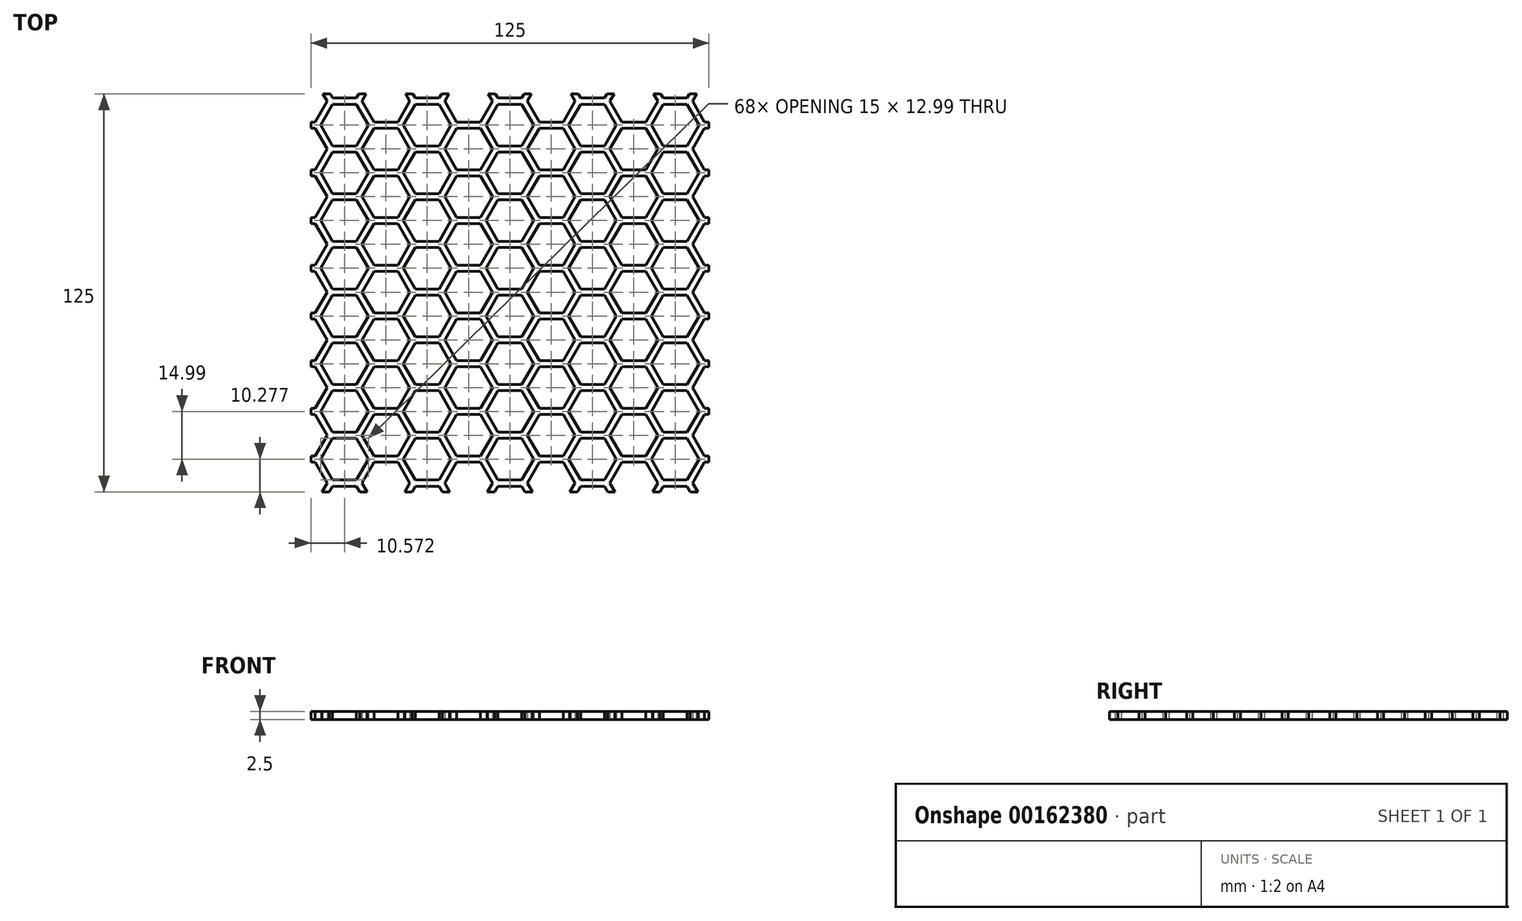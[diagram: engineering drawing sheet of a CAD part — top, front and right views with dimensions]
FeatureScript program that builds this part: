
annotation { "Feature Type Name" : "Feature", "Feature Type Description" : "" }
export const myFeature = defineFeature(function(context is Context, id is Id, definition is map)
    precondition{}
    {
        {
            var Q0;
            Q0=qCreatedBy(makeId("Top.planeOp"),FACE);
            var sketch = newSketch(context, id + "F0", { "sketchPlane" : qUnion([Q0])});
            skPoint(sketch, "E0.middle", {"position": v(0, 0) * mm});
            skLineSegment(sketch, "E1.bottom", {"start": v(60, 62.5) * mm, "end": v(-60, 62.5) * mm});
            skLineSegment(sketch, "E1.top", {"start": v(60, -62.5) * mm, "end": v(-60, -62.5) * mm});
            skLineSegment(sketch, "E1.left", {"start": v(62.5, 60) * mm, "end": v(62.5, -60) * mm});
            skLineSegment(sketch, "E1.right", {"start": v(-62.5, 60) * mm, "end": v(-62.5, -60) * mm});
            skArc(sketch, "E2", {"start": v(-60, 62.5) * mm, "mid": v(-61.77, 61.77) * mm, "end": v(-62.5, 60) * mm});
            skArc(sketch, "E3", {"start": v(62.5, 60) * mm, "mid": v(61.77, 61.77) * mm, "end": v(60, 62.5) * mm});
            skArc(sketch, "E4", {"start": v(60, -62.5) * mm, "mid": v(61.77, -61.77) * mm, "end": v(62.5, -60) * mm});
            skArc(sketch, "E5", {"start": v(-62.5, -60) * mm, "mid": v(-61.77, -61.77) * mm, "end": v(-60, -62.5) * mm});
            skLineSegment(sketch, "E6", {"start": v(0, 0) * mm, "end": v(0, 62.5) * mm, "construction": true});
            skLineSegment(sketch, "E7", {"start": v(0, 0) * mm, "end": v(0, -62.5) * mm, "construction": true});
            skSolve(sketch);
        }
        {
            var Q0;
            Q0=makeQuery(id+"F0.imprint","IMPRINT",FACE,{"disambiguationData":[TD([[makeQuery(id+"F0.imprint","IMPRINT",EDGE,{"derivedFrom":sQuery(id+"F0.wireOp",EDGE,"E1.bottom")}),1.0]])]});
            extrude(context, id + "F1", {"entities" : qUnion([Q0]), "offsetDistance" : 25 * mm, "depth" : 2.5 * mm});
        }
        {
            var Q0;
            Q0=qCreatedBy(makeId("Top.planeOp"),FACE);
            var sketch = newSketch(context, id + "F2", { "sketchPlane" : qUnion([Q0])});
            skCircle(sketch, "E8.cCircle", {"center": v(-25.96, -52.22) * mm, "radius": 7.5 * mm, "construction": true});
            skLineSegment(sketch, "E8.0", {"start": v(-18.46, -52.22) * mm, "end": v(-22.21, -58.72) * mm});
            skLineSegment(sketch, "E8.1", {"start": v(-22.21, -58.72) * mm, "end": v(-29.71, -58.72) * mm});
            skLineSegment(sketch, "E8.2", {"start": v(-29.71, -58.72) * mm, "end": v(-33.46, -52.22) * mm});
            skLineSegment(sketch, "E8.3", {"start": v(-33.46, -52.22) * mm, "end": v(-29.71, -45.73) * mm});
            skLineSegment(sketch, "E8.4", {"start": v(-29.71, -45.73) * mm, "end": v(-22.21, -45.73) * mm});
            skLineSegment(sketch, "E8.5", {"start": v(-22.21, -45.73) * mm, "end": v(-18.46, -52.22) * mm});
            skCircle(sketch, "E9.cCircle", {"center": v(-38.95, -59.72) * mm, "radius": 7.5 * mm, "construction": true});
            skLineSegment(sketch, "E9.0", {"start": v(-42.7, -53.22) * mm, "end": v(-35.2, -53.22) * mm});
            skLineSegment(sketch, "E9.1", {"start": v(-35.2, -53.22) * mm, "end": v(-31.45, -59.72) * mm});
            skLineSegment(sketch, "E9.2", {"start": v(-31.45, -59.72) * mm, "end": v(-35.2, -66.21) * mm});
            skLineSegment(sketch, "E9.3", {"start": v(-35.2, -66.21) * mm, "end": v(-42.7, -66.21) * mm});
            skLineSegment(sketch, "E9.4", {"start": v(-42.7, -66.21) * mm, "end": v(-46.45, -59.72) * mm});
            skLineSegment(sketch, "E9.5", {"start": v(-46.45, -59.72) * mm, "end": v(-42.7, -53.22) * mm});
            skLineSegment(sketch, "E10", {"start": v(-38.95, -59.72) * mm, "end": v(-25.96, -52.22) * mm, "construction": true});
            skCircle(sketch, "E11.MirrorC", {"center": v(-12.98, -59.72) * mm, "radius": 7.5 * mm, "construction": true});
            skLineSegment(sketch, "E12.MirrorCS", {"start": v(-20.48, -59.72) * mm, "end": v(-16.73, -66.21) * mm});
            skLineSegment(sketch, "E13.MirrorCS", {"start": v(-16.73, -66.21) * mm, "end": v(-9.23, -66.21) * mm});
            skLineSegment(sketch, "E14.MirrorCS", {"start": v(-9.23, -66.21) * mm, "end": v(-5.48, -59.72) * mm});
            skLineSegment(sketch, "E15.MirrorCS", {"start": v(-5.48, -59.72) * mm, "end": v(-9.23, -53.22) * mm});
            skLineSegment(sketch, "E16.MirrorCS", {"start": v(-9.23, -53.22) * mm, "end": v(-16.73, -53.22) * mm});
            skLineSegment(sketch, "E17.MirrorCS", {"start": v(-16.73, -53.22) * mm, "end": v(-20.48, -59.72) * mm});
            skLineSegment(sketch, "E18.MirrorCS", {"start": v(-12.98, -59.72) * mm, "end": v(-25.96, -52.22) * mm, "construction": true});
            skLineSegment(sketch, "E19.1.0.0", {"start": v(12.98, -59.72) * mm, "end": v(0, -52.22) * mm, "construction": true});
            skLineSegment(sketch, "E19.1.0.1", {"start": v(3.75, -45.73) * mm, "end": v(7.5, -52.22) * mm});
            skLineSegment(sketch, "E19.1.0.2", {"start": v(-12.98, -59.72) * mm, "end": v(0, -52.22) * mm, "construction": true});
            skLineSegment(sketch, "E19.1.0.3", {"start": v(-3.75, -45.73) * mm, "end": v(3.75, -45.73) * mm});
            skLineSegment(sketch, "E19.1.0.4", {"start": v(16.73, -66.21) * mm, "end": v(20.48, -59.72) * mm});
            skLineSegment(sketch, "E19.1.0.5", {"start": v(20.48, -59.72) * mm, "end": v(16.73, -53.22) * mm});
            skLineSegment(sketch, "E19.1.0.6", {"start": v(5.48, -59.72) * mm, "end": v(9.23, -66.21) * mm});
            skCircle(sketch, "E19.1.0.7", {"center": v(0, -52.22) * mm, "radius": 7.5 * mm, "construction": true});
            skLineSegment(sketch, "E19.1.0.8", {"start": v(9.23, -53.22) * mm, "end": v(5.48, -59.72) * mm});
            skLineSegment(sketch, "E19.1.0.9", {"start": v(7.5, -52.22) * mm, "end": v(3.75, -58.72) * mm});
            skLineSegment(sketch, "E19.1.0.10", {"start": v(9.23, -66.21) * mm, "end": v(16.73, -66.21) * mm});
            skLineSegment(sketch, "E19.1.0.11", {"start": v(3.75, -58.72) * mm, "end": v(-3.75, -58.72) * mm});
            skLineSegment(sketch, "E19.1.0.12", {"start": v(-3.75, -58.72) * mm, "end": v(-7.5, -52.22) * mm});
            skLineSegment(sketch, "E19.1.0.13", {"start": v(16.73, -53.22) * mm, "end": v(9.23, -53.22) * mm});
            skLineSegment(sketch, "E19.1.0.14", {"start": v(-7.5, -52.22) * mm, "end": v(-3.75, -45.73) * mm});
            skCircle(sketch, "E19.1.0.15", {"center": v(12.98, -59.72) * mm, "radius": 7.5 * mm, "construction": true});
            skLineSegment(sketch, "E19.direction1", {"start": v(-38.95, -59.72) * mm, "end": v(-12.98, -59.72) * mm, "construction": true});
            skCircle(sketch, "E20.MirrorC", {"center": v(-51.93, -52.22) * mm, "radius": 7.5 * mm, "construction": true});
            skLineSegment(sketch, "E21.MirrorCS", {"start": v(-61.16, -66.21) * mm, "end": v(-68.66, -66.21) * mm});
            skLineSegment(sketch, "E22.MirrorCS", {"start": v(-38.95, -59.72) * mm, "end": v(-51.93, -52.22) * mm, "construction": true});
            skLineSegment(sketch, "E23.MirrorCS", {"start": v(-64.91, -59.72) * mm, "end": v(-51.93, -52.22) * mm, "construction": true});
            skLineSegment(sketch, "E24.MirrorCS", {"start": v(-72.41, -59.72) * mm, "end": v(-68.66, -53.22) * mm});
            skCircle(sketch, "E25.MirrorC", {"center": v(-64.91, -59.72) * mm, "radius": 7.5 * mm, "construction": true});
            skLineSegment(sketch, "E26.MirrorCS", {"start": v(-61.16, -53.22) * mm, "end": v(-57.41, -59.72) * mm});
            skLineSegment(sketch, "E27.MirrorCS", {"start": v(-55.68, -58.72) * mm, "end": v(-48.18, -58.72) * mm});
            skLineSegment(sketch, "E28.MirrorCS", {"start": v(-48.18, -45.73) * mm, "end": v(-55.68, -45.73) * mm});
            skLineSegment(sketch, "E29.MirrorCS", {"start": v(-48.18, -58.72) * mm, "end": v(-44.43, -52.22) * mm});
            skLineSegment(sketch, "E30.MirrorCS", {"start": v(-44.43, -52.22) * mm, "end": v(-48.18, -45.73) * mm});
            skLineSegment(sketch, "E31.MirrorCS", {"start": v(-57.41, -59.72) * mm, "end": v(-61.16, -66.21) * mm});
            skLineSegment(sketch, "E32.MirrorCS", {"start": v(-68.66, -66.21) * mm, "end": v(-72.41, -59.72) * mm});
            skLineSegment(sketch, "E33.MirrorCS", {"start": v(-59.43, -52.22) * mm, "end": v(-55.68, -58.72) * mm});
            skLineSegment(sketch, "E34.MirrorCS", {"start": v(-55.68, -45.73) * mm, "end": v(-59.43, -52.22) * mm});
            skLineSegment(sketch, "E35.MirrorCS", {"start": v(-68.66, -53.22) * mm, "end": v(-61.16, -53.22) * mm});
            skLineSegment(sketch, "E36.0.1.0", {"start": v(-29.71, -30.74) * mm, "end": v(-22.21, -30.74) * mm});
            skLineSegment(sketch, "E36.0.1.1", {"start": v(-33.46, -37.23) * mm, "end": v(-29.71, -30.74) * mm});
            skLineSegment(sketch, "E36.0.1.2", {"start": v(-18.46, -37.23) * mm, "end": v(-22.21, -43.73) * mm});
            skLineSegment(sketch, "E36.0.1.3", {"start": v(-46.45, -44.73) * mm, "end": v(-42.7, -38.23) * mm});
            skCircle(sketch, "E36.0.1.4", {"center": v(-51.93, -37.23) * mm, "radius": 7.5 * mm, "construction": true});
            skLineSegment(sketch, "E36.0.1.5", {"start": v(9.23, -38.23) * mm, "end": v(5.48, -44.73) * mm});
            skLineSegment(sketch, "E36.0.1.6", {"start": v(-12.98, -44.73) * mm, "end": v(-25.96, -37.23) * mm, "construction": true});
            skCircle(sketch, "E36.0.1.7", {"center": v(12.98, -44.73) * mm, "radius": 7.5 * mm, "construction": true});
            skLineSegment(sketch, "E36.0.1.8", {"start": v(-38.95, -44.73) * mm, "end": v(-25.96, -37.23) * mm, "construction": true});
            skLineSegment(sketch, "E36.0.1.9", {"start": v(-16.73, -38.23) * mm, "end": v(-20.48, -44.73) * mm});
            skCircle(sketch, "E36.0.1.10", {"center": v(-64.91, -44.73) * mm, "radius": 7.5 * mm, "construction": true});
            skLineSegment(sketch, "E36.0.1.11", {"start": v(-31.45, -44.73) * mm, "end": v(-35.2, -51.22) * mm});
            skLineSegment(sketch, "E36.0.1.12", {"start": v(7.5, -37.23) * mm, "end": v(3.75, -43.73) * mm});
            skLineSegment(sketch, "E36.0.1.13", {"start": v(9.23, -51.22) * mm, "end": v(16.73, -51.22) * mm});
            skLineSegment(sketch, "E36.0.1.14", {"start": v(3.75, -43.73) * mm, "end": v(-3.75, -43.73) * mm});
            skLineSegment(sketch, "E36.0.1.15", {"start": v(-12.98, -44.73) * mm, "end": v(0, -37.23) * mm, "construction": true});
            skCircle(sketch, "E36.0.1.16", {"center": v(-25.96, -37.23) * mm, "radius": 7.5 * mm, "construction": true});
            skCircle(sketch, "E36.0.1.17", {"center": v(-38.95, -44.73) * mm, "radius": 7.5 * mm, "construction": true});
            skLineSegment(sketch, "E36.0.1.18", {"start": v(-42.7, -38.23) * mm, "end": v(-35.2, -38.23) * mm});
            skLineSegment(sketch, "E36.0.1.19", {"start": v(-29.71, -43.73) * mm, "end": v(-33.46, -37.23) * mm});
            skLineSegment(sketch, "E36.0.1.20", {"start": v(-22.21, -30.74) * mm, "end": v(-18.46, -37.23) * mm});
            skLineSegment(sketch, "E36.0.1.21", {"start": v(-48.18, -43.73) * mm, "end": v(-44.43, -37.23) * mm});
            skLineSegment(sketch, "E36.0.1.22", {"start": v(-57.41, -44.73) * mm, "end": v(-61.16, -51.22) * mm});
            skLineSegment(sketch, "E36.0.1.23", {"start": v(-9.23, -38.23) * mm, "end": v(-16.73, -38.23) * mm});
            skLineSegment(sketch, "E36.0.1.24", {"start": v(3.75, -30.74) * mm, "end": v(7.5, -37.23) * mm});
            skLineSegment(sketch, "E36.0.1.25", {"start": v(20.48, -44.73) * mm, "end": v(16.73, -38.23) * mm});
            skLineSegment(sketch, "E36.0.1.26", {"start": v(16.73, -51.22) * mm, "end": v(20.48, -44.73) * mm});
            skLineSegment(sketch, "E36.0.1.27", {"start": v(-20.48, -44.73) * mm, "end": v(-16.73, -51.22) * mm});
            skLineSegment(sketch, "E36.0.1.28", {"start": v(-72.41, -44.73) * mm, "end": v(-68.66, -38.23) * mm});
            skLineSegment(sketch, "E36.0.1.29", {"start": v(5.48, -44.73) * mm, "end": v(9.23, -51.22) * mm});
            skLineSegment(sketch, "E36.0.1.30", {"start": v(-9.23, -51.22) * mm, "end": v(-5.48, -44.73) * mm});
            skLineSegment(sketch, "E36.0.1.31", {"start": v(-42.7, -51.22) * mm, "end": v(-46.45, -44.73) * mm});
            skLineSegment(sketch, "E36.0.1.32", {"start": v(-55.68, -43.73) * mm, "end": v(-48.18, -43.73) * mm});
            skLineSegment(sketch, "E36.0.1.33", {"start": v(-5.48, -44.73) * mm, "end": v(-9.23, -38.23) * mm});
            skLineSegment(sketch, "E36.0.1.34", {"start": v(-38.95, -44.73) * mm, "end": v(-51.93, -37.23) * mm, "construction": true});
            skLineSegment(sketch, "E36.0.1.35", {"start": v(-44.43, -37.23) * mm, "end": v(-48.18, -30.74) * mm});
            skLineSegment(sketch, "E36.0.1.36", {"start": v(16.73, -38.23) * mm, "end": v(9.23, -38.23) * mm});
            skLineSegment(sketch, "E36.0.1.37", {"start": v(-48.18, -30.74) * mm, "end": v(-55.68, -30.74) * mm});
            skLineSegment(sketch, "E36.0.1.38", {"start": v(-61.16, -38.23) * mm, "end": v(-57.41, -44.73) * mm});
            skLineSegment(sketch, "E36.0.1.39", {"start": v(-35.2, -51.22) * mm, "end": v(-42.7, -51.22) * mm});
            skLineSegment(sketch, "E36.0.1.40", {"start": v(-3.75, -30.74) * mm, "end": v(3.75, -30.74) * mm});
            skLineSegment(sketch, "E36.0.1.41", {"start": v(-3.75, -43.73) * mm, "end": v(-7.5, -37.23) * mm});
            skLineSegment(sketch, "E36.0.1.42", {"start": v(-22.21, -43.73) * mm, "end": v(-29.71, -43.73) * mm});
            skLineSegment(sketch, "E36.0.1.43", {"start": v(12.98, -44.73) * mm, "end": v(0, -37.23) * mm, "construction": true});
            skCircle(sketch, "E36.0.1.44", {"center": v(-12.98, -44.73) * mm, "radius": 7.5 * mm, "construction": true});
            skLineSegment(sketch, "E36.0.1.45", {"start": v(-55.68, -30.74) * mm, "end": v(-59.43, -37.23) * mm});
            skCircle(sketch, "E36.0.1.46", {"center": v(0, -37.23) * mm, "radius": 7.5 * mm, "construction": true});
            skLineSegment(sketch, "E36.0.1.47", {"start": v(-7.5, -37.23) * mm, "end": v(-3.75, -30.74) * mm});
            skLineSegment(sketch, "E36.0.1.48", {"start": v(-61.16, -51.22) * mm, "end": v(-68.66, -51.22) * mm});
            skLineSegment(sketch, "E36.0.1.49", {"start": v(-16.73, -51.22) * mm, "end": v(-9.23, -51.22) * mm});
            skLineSegment(sketch, "E36.0.1.50", {"start": v(-59.43, -37.23) * mm, "end": v(-55.68, -43.73) * mm});
            skLineSegment(sketch, "E36.0.1.51", {"start": v(-68.66, -38.23) * mm, "end": v(-61.16, -38.23) * mm});
            skLineSegment(sketch, "E36.0.1.52", {"start": v(-68.66, -51.22) * mm, "end": v(-72.41, -44.73) * mm});
            skLineSegment(sketch, "E36.0.1.53", {"start": v(-64.91, -44.73) * mm, "end": v(-51.93, -37.23) * mm, "construction": true});
            skLineSegment(sketch, "E36.0.1.54", {"start": v(-38.95, -44.73) * mm, "end": v(-12.98, -44.73) * mm, "construction": true});
            skLineSegment(sketch, "E36.0.1.55", {"start": v(-35.2, -38.23) * mm, "end": v(-31.45, -44.73) * mm});
            skLineSegment(sketch, "E36.0.2.0", {"start": v(-29.71, -15.75) * mm, "end": v(-22.21, -15.75) * mm});
            skLineSegment(sketch, "E36.0.2.1", {"start": v(-33.46, -22.24) * mm, "end": v(-29.71, -15.75) * mm});
            skLineSegment(sketch, "E36.0.2.2", {"start": v(-18.46, -22.24) * mm, "end": v(-22.21, -28.74) * mm});
            skLineSegment(sketch, "E36.0.2.3", {"start": v(-46.45, -29.74) * mm, "end": v(-42.7, -23.24) * mm});
            skCircle(sketch, "E36.0.2.4", {"center": v(-51.93, -22.24) * mm, "radius": 7.5 * mm, "construction": true});
            skLineSegment(sketch, "E36.0.2.5", {"start": v(9.23, -23.24) * mm, "end": v(5.48, -29.74) * mm});
            skLineSegment(sketch, "E36.0.2.6", {"start": v(-12.98, -29.74) * mm, "end": v(-25.96, -22.24) * mm, "construction": true});
            skCircle(sketch, "E36.0.2.7", {"center": v(12.98, -29.74) * mm, "radius": 7.5 * mm, "construction": true});
            skLineSegment(sketch, "E36.0.2.8", {"start": v(-38.95, -29.74) * mm, "end": v(-25.96, -22.24) * mm, "construction": true});
            skLineSegment(sketch, "E36.0.2.9", {"start": v(-16.73, -23.24) * mm, "end": v(-20.48, -29.74) * mm});
            skCircle(sketch, "E36.0.2.10", {"center": v(-64.91, -29.74) * mm, "radius": 7.5 * mm, "construction": true});
            skLineSegment(sketch, "E36.0.2.11", {"start": v(-31.45, -29.74) * mm, "end": v(-35.2, -36.23) * mm});
            skLineSegment(sketch, "E36.0.2.12", {"start": v(7.5, -22.24) * mm, "end": v(3.75, -28.74) * mm});
            skLineSegment(sketch, "E36.0.2.13", {"start": v(9.23, -36.23) * mm, "end": v(16.73, -36.23) * mm});
            skLineSegment(sketch, "E36.0.2.14", {"start": v(3.75, -28.74) * mm, "end": v(-3.75, -28.74) * mm});
            skLineSegment(sketch, "E36.0.2.15", {"start": v(-12.98, -29.74) * mm, "end": v(0, -22.24) * mm, "construction": true});
            skCircle(sketch, "E36.0.2.16", {"center": v(-25.96, -22.24) * mm, "radius": 7.5 * mm, "construction": true});
            skCircle(sketch, "E36.0.2.17", {"center": v(-38.95, -29.74) * mm, "radius": 7.5 * mm, "construction": true});
            skLineSegment(sketch, "E36.0.2.18", {"start": v(-42.7, -23.24) * mm, "end": v(-35.2, -23.24) * mm});
            skLineSegment(sketch, "E36.0.2.19", {"start": v(-29.71, -28.74) * mm, "end": v(-33.46, -22.24) * mm});
            skLineSegment(sketch, "E36.0.2.20", {"start": v(-22.21, -15.75) * mm, "end": v(-18.46, -22.24) * mm});
            skLineSegment(sketch, "E36.0.2.21", {"start": v(-48.18, -28.74) * mm, "end": v(-44.43, -22.24) * mm});
            skLineSegment(sketch, "E36.0.2.22", {"start": v(-57.41, -29.74) * mm, "end": v(-61.16, -36.23) * mm});
            skLineSegment(sketch, "E36.0.2.23", {"start": v(-9.23, -23.24) * mm, "end": v(-16.73, -23.24) * mm});
            skLineSegment(sketch, "E36.0.2.24", {"start": v(3.75, -15.75) * mm, "end": v(7.5, -22.24) * mm});
            skLineSegment(sketch, "E36.0.2.25", {"start": v(20.48, -29.74) * mm, "end": v(16.73, -23.24) * mm});
            skLineSegment(sketch, "E36.0.2.26", {"start": v(16.73, -36.23) * mm, "end": v(20.48, -29.74) * mm});
            skLineSegment(sketch, "E36.0.2.27", {"start": v(-20.48, -29.74) * mm, "end": v(-16.73, -36.23) * mm});
            skLineSegment(sketch, "E36.0.2.28", {"start": v(-72.41, -29.74) * mm, "end": v(-68.66, -23.24) * mm});
            skLineSegment(sketch, "E36.0.2.29", {"start": v(5.48, -29.74) * mm, "end": v(9.23, -36.23) * mm});
            skLineSegment(sketch, "E36.0.2.30", {"start": v(-9.23, -36.23) * mm, "end": v(-5.48, -29.74) * mm});
            skLineSegment(sketch, "E36.0.2.31", {"start": v(-42.7, -36.23) * mm, "end": v(-46.45, -29.74) * mm});
            skLineSegment(sketch, "E36.0.2.32", {"start": v(-55.68, -28.74) * mm, "end": v(-48.18, -28.74) * mm});
            skLineSegment(sketch, "E36.0.2.33", {"start": v(-5.48, -29.74) * mm, "end": v(-9.23, -23.24) * mm});
            skLineSegment(sketch, "E36.0.2.34", {"start": v(-38.95, -29.74) * mm, "end": v(-51.93, -22.24) * mm, "construction": true});
            skLineSegment(sketch, "E36.0.2.35", {"start": v(-44.43, -22.24) * mm, "end": v(-48.18, -15.75) * mm});
            skLineSegment(sketch, "E36.0.2.36", {"start": v(16.73, -23.24) * mm, "end": v(9.23, -23.24) * mm});
            skLineSegment(sketch, "E36.0.2.37", {"start": v(-48.18, -15.75) * mm, "end": v(-55.68, -15.75) * mm});
            skLineSegment(sketch, "E36.0.2.38", {"start": v(-61.16, -23.24) * mm, "end": v(-57.41, -29.74) * mm});
            skLineSegment(sketch, "E36.0.2.39", {"start": v(-35.2, -36.23) * mm, "end": v(-42.7, -36.23) * mm});
            skLineSegment(sketch, "E36.0.2.40", {"start": v(-3.75, -15.75) * mm, "end": v(3.75, -15.75) * mm});
            skLineSegment(sketch, "E36.0.2.41", {"start": v(-3.75, -28.74) * mm, "end": v(-7.5, -22.24) * mm});
            skLineSegment(sketch, "E36.0.2.42", {"start": v(-22.21, -28.74) * mm, "end": v(-29.71, -28.74) * mm});
            skLineSegment(sketch, "E36.0.2.43", {"start": v(12.98, -29.74) * mm, "end": v(0, -22.24) * mm, "construction": true});
            skCircle(sketch, "E36.0.2.44", {"center": v(-12.98, -29.74) * mm, "radius": 7.5 * mm, "construction": true});
            skLineSegment(sketch, "E36.0.2.45", {"start": v(-55.68, -15.75) * mm, "end": v(-59.43, -22.24) * mm});
            skCircle(sketch, "E36.0.2.46", {"center": v(0, -22.24) * mm, "radius": 7.5 * mm, "construction": true});
            skLineSegment(sketch, "E36.0.2.47", {"start": v(-7.5, -22.24) * mm, "end": v(-3.75, -15.75) * mm});
            skLineSegment(sketch, "E36.0.2.48", {"start": v(-61.16, -36.23) * mm, "end": v(-68.66, -36.23) * mm});
            skLineSegment(sketch, "E36.0.2.49", {"start": v(-16.73, -36.23) * mm, "end": v(-9.23, -36.23) * mm});
            skLineSegment(sketch, "E36.0.2.50", {"start": v(-59.43, -22.24) * mm, "end": v(-55.68, -28.74) * mm});
            skLineSegment(sketch, "E36.0.2.51", {"start": v(-68.66, -23.24) * mm, "end": v(-61.16, -23.24) * mm});
            skLineSegment(sketch, "E36.0.2.52", {"start": v(-68.66, -36.23) * mm, "end": v(-72.41, -29.74) * mm});
            skLineSegment(sketch, "E36.0.2.53", {"start": v(-64.91, -29.74) * mm, "end": v(-51.93, -22.24) * mm, "construction": true});
            skLineSegment(sketch, "E36.0.2.54", {"start": v(-38.95, -29.74) * mm, "end": v(-12.98, -29.74) * mm, "construction": true});
            skLineSegment(sketch, "E36.0.2.55", {"start": v(-35.2, -23.24) * mm, "end": v(-31.45, -29.74) * mm});
            skLineSegment(sketch, "E36.0.3.0", {"start": v(-29.71, -0.76) * mm, "end": v(-22.21, -0.76) * mm});
            skLineSegment(sketch, "E36.0.3.1", {"start": v(-33.46, -7.25) * mm, "end": v(-29.71, -0.76) * mm});
            skLineSegment(sketch, "E36.0.3.2", {"start": v(-18.46, -7.25) * mm, "end": v(-22.21, -13.75) * mm});
            skLineSegment(sketch, "E36.0.3.3", {"start": v(-46.45, -14.75) * mm, "end": v(-42.7, -8.25) * mm});
            skCircle(sketch, "E36.0.3.4", {"center": v(-51.93, -7.25) * mm, "radius": 7.5 * mm, "construction": true});
            skLineSegment(sketch, "E36.0.3.5", {"start": v(9.23, -8.25) * mm, "end": v(5.48, -14.75) * mm});
            skLineSegment(sketch, "E36.0.3.6", {"start": v(-12.98, -14.75) * mm, "end": v(-25.96, -7.25) * mm, "construction": true});
            skCircle(sketch, "E36.0.3.7", {"center": v(12.98, -14.75) * mm, "radius": 7.5 * mm, "construction": true});
            skLineSegment(sketch, "E36.0.3.8", {"start": v(-38.95, -14.75) * mm, "end": v(-25.96, -7.25) * mm, "construction": true});
            skLineSegment(sketch, "E36.0.3.9", {"start": v(-16.73, -8.25) * mm, "end": v(-20.48, -14.75) * mm});
            skCircle(sketch, "E36.0.3.10", {"center": v(-64.91, -14.75) * mm, "radius": 7.5 * mm, "construction": true});
            skLineSegment(sketch, "E36.0.3.11", {"start": v(-31.45, -14.75) * mm, "end": v(-35.2, -21.24) * mm});
            skLineSegment(sketch, "E36.0.3.12", {"start": v(7.5, -7.25) * mm, "end": v(3.75, -13.75) * mm});
            skLineSegment(sketch, "E36.0.3.13", {"start": v(9.23, -21.24) * mm, "end": v(16.73, -21.24) * mm});
            skLineSegment(sketch, "E36.0.3.14", {"start": v(3.75, -13.75) * mm, "end": v(-3.75, -13.75) * mm});
            skLineSegment(sketch, "E36.0.3.15", {"start": v(-12.98, -14.75) * mm, "end": v(0, -7.25) * mm, "construction": true});
            skCircle(sketch, "E36.0.3.16", {"center": v(-25.96, -7.25) * mm, "radius": 7.5 * mm, "construction": true});
            skCircle(sketch, "E36.0.3.17", {"center": v(-38.95, -14.75) * mm, "radius": 7.5 * mm, "construction": true});
            skLineSegment(sketch, "E36.0.3.18", {"start": v(-42.7, -8.25) * mm, "end": v(-35.2, -8.25) * mm});
            skLineSegment(sketch, "E36.0.3.19", {"start": v(-29.71, -13.75) * mm, "end": v(-33.46, -7.25) * mm});
            skLineSegment(sketch, "E36.0.3.20", {"start": v(-22.21, -0.76) * mm, "end": v(-18.46, -7.25) * mm});
            skLineSegment(sketch, "E36.0.3.21", {"start": v(-48.18, -13.75) * mm, "end": v(-44.43, -7.25) * mm});
            skLineSegment(sketch, "E36.0.3.22", {"start": v(-57.41, -14.75) * mm, "end": v(-61.16, -21.24) * mm});
            skLineSegment(sketch, "E36.0.3.23", {"start": v(-9.23, -8.25) * mm, "end": v(-16.73, -8.25) * mm});
            skLineSegment(sketch, "E36.0.3.24", {"start": v(3.75, -0.76) * mm, "end": v(7.5, -7.25) * mm});
            skLineSegment(sketch, "E36.0.3.25", {"start": v(20.48, -14.75) * mm, "end": v(16.73, -8.25) * mm});
            skLineSegment(sketch, "E36.0.3.26", {"start": v(16.73, -21.24) * mm, "end": v(20.48, -14.75) * mm});
            skLineSegment(sketch, "E36.0.3.27", {"start": v(-20.48, -14.75) * mm, "end": v(-16.73, -21.24) * mm});
            skLineSegment(sketch, "E36.0.3.28", {"start": v(-72.41, -14.75) * mm, "end": v(-68.66, -8.25) * mm});
            skLineSegment(sketch, "E36.0.3.29", {"start": v(5.48, -14.75) * mm, "end": v(9.23, -21.24) * mm});
            skLineSegment(sketch, "E36.0.3.30", {"start": v(-9.23, -21.24) * mm, "end": v(-5.48, -14.75) * mm});
            skLineSegment(sketch, "E36.0.3.31", {"start": v(-42.7, -21.24) * mm, "end": v(-46.45, -14.75) * mm});
            skLineSegment(sketch, "E36.0.3.32", {"start": v(-55.68, -13.75) * mm, "end": v(-48.18, -13.75) * mm});
            skLineSegment(sketch, "E36.0.3.33", {"start": v(-5.48, -14.75) * mm, "end": v(-9.23, -8.25) * mm});
            skLineSegment(sketch, "E36.0.3.34", {"start": v(-38.95, -14.75) * mm, "end": v(-51.93, -7.25) * mm, "construction": true});
            skLineSegment(sketch, "E36.0.3.35", {"start": v(-44.43, -7.25) * mm, "end": v(-48.18, -0.76) * mm});
            skLineSegment(sketch, "E36.0.3.36", {"start": v(16.73, -8.25) * mm, "end": v(9.23, -8.25) * mm});
            skLineSegment(sketch, "E36.0.3.37", {"start": v(-48.18, -0.76) * mm, "end": v(-55.68, -0.76) * mm});
            skLineSegment(sketch, "E36.0.3.38", {"start": v(-61.16, -8.25) * mm, "end": v(-57.41, -14.75) * mm});
            skLineSegment(sketch, "E36.0.3.39", {"start": v(-35.2, -21.24) * mm, "end": v(-42.7, -21.24) * mm});
            skLineSegment(sketch, "E36.0.3.40", {"start": v(-3.75, -0.76) * mm, "end": v(3.75, -0.76) * mm});
            skLineSegment(sketch, "E36.0.3.41", {"start": v(-3.75, -13.75) * mm, "end": v(-7.5, -7.25) * mm});
            skLineSegment(sketch, "E36.0.3.42", {"start": v(-22.21, -13.75) * mm, "end": v(-29.71, -13.75) * mm});
            skLineSegment(sketch, "E36.0.3.43", {"start": v(12.98, -14.75) * mm, "end": v(0, -7.25) * mm, "construction": true});
            skCircle(sketch, "E36.0.3.44", {"center": v(-12.98, -14.75) * mm, "radius": 7.5 * mm, "construction": true});
            skLineSegment(sketch, "E36.0.3.45", {"start": v(-55.68, -0.76) * mm, "end": v(-59.43, -7.25) * mm});
            skCircle(sketch, "E36.0.3.46", {"center": v(0, -7.25) * mm, "radius": 7.5 * mm, "construction": true});
            skLineSegment(sketch, "E36.0.3.47", {"start": v(-7.5, -7.25) * mm, "end": v(-3.75, -0.76) * mm});
            skLineSegment(sketch, "E36.0.3.48", {"start": v(-61.16, -21.24) * mm, "end": v(-68.66, -21.24) * mm});
            skLineSegment(sketch, "E36.0.3.49", {"start": v(-16.73, -21.24) * mm, "end": v(-9.23, -21.24) * mm});
            skLineSegment(sketch, "E36.0.3.50", {"start": v(-59.43, -7.25) * mm, "end": v(-55.68, -13.75) * mm});
            skLineSegment(sketch, "E36.0.3.51", {"start": v(-68.66, -8.25) * mm, "end": v(-61.16, -8.25) * mm});
            skLineSegment(sketch, "E36.0.3.52", {"start": v(-68.66, -21.24) * mm, "end": v(-72.41, -14.75) * mm});
            skLineSegment(sketch, "E36.0.3.53", {"start": v(-64.91, -14.75) * mm, "end": v(-51.93, -7.25) * mm, "construction": true});
            skLineSegment(sketch, "E36.0.3.54", {"start": v(-38.95, -14.75) * mm, "end": v(-12.98, -14.75) * mm, "construction": true});
            skLineSegment(sketch, "E36.0.3.55", {"start": v(-35.2, -8.25) * mm, "end": v(-31.45, -14.75) * mm});
            skLineSegment(sketch, "E36.0.4.0", {"start": v(-29.71, 14.23) * mm, "end": v(-22.21, 14.23) * mm});
            skLineSegment(sketch, "E36.0.4.1", {"start": v(-33.46, 7.74) * mm, "end": v(-29.71, 14.23) * mm});
            skLineSegment(sketch, "E36.0.4.2", {"start": v(-18.46, 7.74) * mm, "end": v(-22.21, 1.24) * mm});
            skLineSegment(sketch, "E36.0.4.3", {"start": v(-46.45, 0.24) * mm, "end": v(-42.7, 6.74) * mm});
            skCircle(sketch, "E36.0.4.4", {"center": v(-51.93, 7.74) * mm, "radius": 7.5 * mm, "construction": true});
            skLineSegment(sketch, "E36.0.4.5", {"start": v(9.23, 6.74) * mm, "end": v(5.48, 0.24) * mm});
            skLineSegment(sketch, "E36.0.4.6", {"start": v(-12.98, 0.24) * mm, "end": v(-25.96, 7.74) * mm, "construction": true});
            skCircle(sketch, "E36.0.4.7", {"center": v(12.98, 0.24) * mm, "radius": 7.5 * mm, "construction": true});
            skLineSegment(sketch, "E36.0.4.8", {"start": v(-38.95, 0.24) * mm, "end": v(-25.96, 7.74) * mm, "construction": true});
            skLineSegment(sketch, "E36.0.4.9", {"start": v(-16.73, 6.74) * mm, "end": v(-20.48, 0.24) * mm});
            skCircle(sketch, "E36.0.4.10", {"center": v(-64.91, 0.24) * mm, "radius": 7.5 * mm, "construction": true});
            skLineSegment(sketch, "E36.0.4.11", {"start": v(-31.45, 0.24) * mm, "end": v(-35.2, -6.25) * mm});
            skLineSegment(sketch, "E36.0.4.12", {"start": v(7.5, 7.74) * mm, "end": v(3.75, 1.24) * mm});
            skLineSegment(sketch, "E36.0.4.13", {"start": v(9.23, -6.25) * mm, "end": v(16.73, -6.25) * mm});
            skLineSegment(sketch, "E36.0.4.14", {"start": v(3.75, 1.24) * mm, "end": v(-3.75, 1.24) * mm});
            skLineSegment(sketch, "E36.0.4.15", {"start": v(-12.98, 0.24) * mm, "end": v(0, 7.74) * mm, "construction": true});
            skCircle(sketch, "E36.0.4.16", {"center": v(-25.96, 7.74) * mm, "radius": 7.5 * mm, "construction": true});
            skCircle(sketch, "E36.0.4.17", {"center": v(-38.95, 0.24) * mm, "radius": 7.5 * mm, "construction": true});
            skLineSegment(sketch, "E36.0.4.18", {"start": v(-42.7, 6.74) * mm, "end": v(-35.2, 6.74) * mm});
            skLineSegment(sketch, "E36.0.4.19", {"start": v(-29.71, 1.24) * mm, "end": v(-33.46, 7.74) * mm});
            skLineSegment(sketch, "E36.0.4.20", {"start": v(-22.21, 14.23) * mm, "end": v(-18.46, 7.74) * mm});
            skLineSegment(sketch, "E36.0.4.21", {"start": v(-48.18, 1.24) * mm, "end": v(-44.43, 7.74) * mm});
            skLineSegment(sketch, "E36.0.4.22", {"start": v(-57.41, 0.24) * mm, "end": v(-61.16, -6.25) * mm});
            skLineSegment(sketch, "E36.0.4.23", {"start": v(-9.23, 6.74) * mm, "end": v(-16.73, 6.74) * mm});
            skLineSegment(sketch, "E36.0.4.24", {"start": v(3.75, 14.23) * mm, "end": v(7.5, 7.74) * mm});
            skLineSegment(sketch, "E36.0.4.25", {"start": v(20.48, 0.24) * mm, "end": v(16.73, 6.74) * mm});
            skLineSegment(sketch, "E36.0.4.26", {"start": v(16.73, -6.25) * mm, "end": v(20.48, 0.24) * mm});
            skLineSegment(sketch, "E36.0.4.27", {"start": v(-20.48, 0.24) * mm, "end": v(-16.73, -6.25) * mm});
            skLineSegment(sketch, "E36.0.4.28", {"start": v(-72.41, 0.24) * mm, "end": v(-68.66, 6.74) * mm});
            skLineSegment(sketch, "E36.0.4.29", {"start": v(5.48, 0.24) * mm, "end": v(9.23, -6.25) * mm});
            skLineSegment(sketch, "E36.0.4.30", {"start": v(-9.23, -6.25) * mm, "end": v(-5.48, 0.24) * mm});
            skLineSegment(sketch, "E36.0.4.31", {"start": v(-42.7, -6.25) * mm, "end": v(-46.45, 0.24) * mm});
            skLineSegment(sketch, "E36.0.4.32", {"start": v(-55.68, 1.24) * mm, "end": v(-48.18, 1.24) * mm});
            skLineSegment(sketch, "E36.0.4.33", {"start": v(-5.48, 0.24) * mm, "end": v(-9.23, 6.74) * mm});
            skLineSegment(sketch, "E36.0.4.34", {"start": v(-38.95, 0.24) * mm, "end": v(-51.93, 7.74) * mm, "construction": true});
            skLineSegment(sketch, "E36.0.4.35", {"start": v(-44.43, 7.74) * mm, "end": v(-48.18, 14.23) * mm});
            skLineSegment(sketch, "E36.0.4.36", {"start": v(16.73, 6.74) * mm, "end": v(9.23, 6.74) * mm});
            skLineSegment(sketch, "E36.0.4.37", {"start": v(-48.18, 14.23) * mm, "end": v(-55.68, 14.23) * mm});
            skLineSegment(sketch, "E36.0.4.38", {"start": v(-61.16, 6.74) * mm, "end": v(-57.41, 0.24) * mm});
            skLineSegment(sketch, "E36.0.4.39", {"start": v(-35.2, -6.25) * mm, "end": v(-42.7, -6.25) * mm});
            skLineSegment(sketch, "E36.0.4.40", {"start": v(-3.75, 14.23) * mm, "end": v(3.75, 14.23) * mm});
            skLineSegment(sketch, "E36.0.4.41", {"start": v(-3.75, 1.24) * mm, "end": v(-7.5, 7.74) * mm});
            skLineSegment(sketch, "E36.0.4.42", {"start": v(-22.21, 1.24) * mm, "end": v(-29.71, 1.24) * mm});
            skLineSegment(sketch, "E36.0.4.43", {"start": v(12.98, 0.24) * mm, "end": v(0, 7.74) * mm, "construction": true});
            skCircle(sketch, "E36.0.4.44", {"center": v(-12.98, 0.24) * mm, "radius": 7.5 * mm, "construction": true});
            skLineSegment(sketch, "E36.0.4.45", {"start": v(-55.68, 14.23) * mm, "end": v(-59.43, 7.74) * mm});
            skCircle(sketch, "E36.0.4.46", {"center": v(0, 7.74) * mm, "radius": 7.5 * mm, "construction": true});
            skLineSegment(sketch, "E36.0.4.47", {"start": v(-7.5, 7.74) * mm, "end": v(-3.75, 14.23) * mm});
            skLineSegment(sketch, "E36.0.4.48", {"start": v(-61.16, -6.25) * mm, "end": v(-68.66, -6.25) * mm});
            skLineSegment(sketch, "E36.0.4.49", {"start": v(-16.73, -6.25) * mm, "end": v(-9.23, -6.25) * mm});
            skLineSegment(sketch, "E36.0.4.50", {"start": v(-59.43, 7.74) * mm, "end": v(-55.68, 1.24) * mm});
            skLineSegment(sketch, "E36.0.4.51", {"start": v(-68.66, 6.74) * mm, "end": v(-61.16, 6.74) * mm});
            skLineSegment(sketch, "E36.0.4.52", {"start": v(-68.66, -6.25) * mm, "end": v(-72.41, 0.24) * mm});
            skLineSegment(sketch, "E36.0.4.53", {"start": v(-64.91, 0.24) * mm, "end": v(-51.93, 7.74) * mm, "construction": true});
            skLineSegment(sketch, "E36.0.4.54", {"start": v(-38.95, 0.24) * mm, "end": v(-12.98, 0.24) * mm, "construction": true});
            skLineSegment(sketch, "E36.0.4.55", {"start": v(-35.2, 6.74) * mm, "end": v(-31.45, 0.24) * mm});
            skLineSegment(sketch, "E36.0.5.0", {"start": v(-29.71, 29.22) * mm, "end": v(-22.21, 29.22) * mm});
            skLineSegment(sketch, "E36.0.5.1", {"start": v(-33.46, 22.73) * mm, "end": v(-29.71, 29.22) * mm});
            skLineSegment(sketch, "E36.0.5.2", {"start": v(-18.46, 22.73) * mm, "end": v(-22.21, 16.23) * mm});
            skLineSegment(sketch, "E36.0.5.3", {"start": v(-46.45, 15.23) * mm, "end": v(-42.7, 21.73) * mm});
            skCircle(sketch, "E36.0.5.4", {"center": v(-51.93, 22.73) * mm, "radius": 7.5 * mm, "construction": true});
            skLineSegment(sketch, "E36.0.5.5", {"start": v(9.23, 21.73) * mm, "end": v(5.48, 15.23) * mm});
            skLineSegment(sketch, "E36.0.5.6", {"start": v(-12.98, 15.23) * mm, "end": v(-25.96, 22.73) * mm, "construction": true});
            skCircle(sketch, "E36.0.5.7", {"center": v(12.98, 15.23) * mm, "radius": 7.5 * mm, "construction": true});
            skLineSegment(sketch, "E36.0.5.8", {"start": v(-38.95, 15.23) * mm, "end": v(-25.96, 22.73) * mm, "construction": true});
            skLineSegment(sketch, "E36.0.5.9", {"start": v(-16.73, 21.73) * mm, "end": v(-20.48, 15.23) * mm});
            skCircle(sketch, "E36.0.5.10", {"center": v(-64.91, 15.23) * mm, "radius": 7.5 * mm, "construction": true});
            skLineSegment(sketch, "E36.0.5.11", {"start": v(-31.45, 15.23) * mm, "end": v(-35.2, 8.74) * mm});
            skLineSegment(sketch, "E36.0.5.12", {"start": v(7.5, 22.73) * mm, "end": v(3.75, 16.23) * mm});
            skLineSegment(sketch, "E36.0.5.13", {"start": v(9.23, 8.74) * mm, "end": v(16.73, 8.74) * mm});
            skLineSegment(sketch, "E36.0.5.14", {"start": v(3.75, 16.23) * mm, "end": v(-3.75, 16.23) * mm});
            skLineSegment(sketch, "E36.0.5.15", {"start": v(-12.98, 15.23) * mm, "end": v(0, 22.73) * mm, "construction": true});
            skCircle(sketch, "E36.0.5.16", {"center": v(-25.96, 22.73) * mm, "radius": 7.5 * mm, "construction": true});
            skCircle(sketch, "E36.0.5.17", {"center": v(-38.95, 15.23) * mm, "radius": 7.5 * mm, "construction": true});
            skLineSegment(sketch, "E36.0.5.18", {"start": v(-42.7, 21.73) * mm, "end": v(-35.2, 21.73) * mm});
            skLineSegment(sketch, "E36.0.5.19", {"start": v(-29.71, 16.23) * mm, "end": v(-33.46, 22.73) * mm});
            skLineSegment(sketch, "E36.0.5.20", {"start": v(-22.21, 29.22) * mm, "end": v(-18.46, 22.73) * mm});
            skLineSegment(sketch, "E36.0.5.21", {"start": v(-48.18, 16.23) * mm, "end": v(-44.43, 22.73) * mm});
            skLineSegment(sketch, "E36.0.5.22", {"start": v(-57.41, 15.23) * mm, "end": v(-61.16, 8.74) * mm});
            skLineSegment(sketch, "E36.0.5.23", {"start": v(-9.23, 21.73) * mm, "end": v(-16.73, 21.73) * mm});
            skLineSegment(sketch, "E36.0.5.24", {"start": v(3.75, 29.22) * mm, "end": v(7.5, 22.73) * mm});
            skLineSegment(sketch, "E36.0.5.25", {"start": v(20.48, 15.23) * mm, "end": v(16.73, 21.73) * mm});
            skLineSegment(sketch, "E36.0.5.26", {"start": v(16.73, 8.74) * mm, "end": v(20.48, 15.23) * mm});
            skLineSegment(sketch, "E36.0.5.27", {"start": v(-20.48, 15.23) * mm, "end": v(-16.73, 8.74) * mm});
            skLineSegment(sketch, "E36.0.5.28", {"start": v(-72.41, 15.23) * mm, "end": v(-68.66, 21.73) * mm});
            skLineSegment(sketch, "E36.0.5.29", {"start": v(5.48, 15.23) * mm, "end": v(9.23, 8.74) * mm});
            skLineSegment(sketch, "E36.0.5.30", {"start": v(-9.23, 8.74) * mm, "end": v(-5.48, 15.23) * mm});
            skLineSegment(sketch, "E36.0.5.31", {"start": v(-42.7, 8.74) * mm, "end": v(-46.45, 15.23) * mm});
            skLineSegment(sketch, "E36.0.5.32", {"start": v(-55.68, 16.23) * mm, "end": v(-48.18, 16.23) * mm});
            skLineSegment(sketch, "E36.0.5.33", {"start": v(-5.48, 15.23) * mm, "end": v(-9.23, 21.73) * mm});
            skLineSegment(sketch, "E36.0.5.34", {"start": v(-38.95, 15.23) * mm, "end": v(-51.93, 22.73) * mm, "construction": true});
            skLineSegment(sketch, "E36.0.5.35", {"start": v(-44.43, 22.73) * mm, "end": v(-48.18, 29.22) * mm});
            skLineSegment(sketch, "E36.0.5.36", {"start": v(16.73, 21.73) * mm, "end": v(9.23, 21.73) * mm});
            skLineSegment(sketch, "E36.0.5.37", {"start": v(-48.18, 29.22) * mm, "end": v(-55.68, 29.22) * mm});
            skLineSegment(sketch, "E36.0.5.38", {"start": v(-61.16, 21.73) * mm, "end": v(-57.41, 15.23) * mm});
            skLineSegment(sketch, "E36.0.5.39", {"start": v(-35.2, 8.74) * mm, "end": v(-42.7, 8.74) * mm});
            skLineSegment(sketch, "E36.0.5.40", {"start": v(-3.75, 29.22) * mm, "end": v(3.75, 29.22) * mm});
            skLineSegment(sketch, "E36.0.5.41", {"start": v(-3.75, 16.23) * mm, "end": v(-7.5, 22.73) * mm});
            skLineSegment(sketch, "E36.0.5.42", {"start": v(-22.21, 16.23) * mm, "end": v(-29.71, 16.23) * mm});
            skLineSegment(sketch, "E36.0.5.43", {"start": v(12.98, 15.23) * mm, "end": v(0, 22.73) * mm, "construction": true});
            skCircle(sketch, "E36.0.5.44", {"center": v(-12.98, 15.23) * mm, "radius": 7.5 * mm, "construction": true});
            skLineSegment(sketch, "E36.0.5.45", {"start": v(-55.68, 29.22) * mm, "end": v(-59.43, 22.73) * mm});
            skCircle(sketch, "E36.0.5.46", {"center": v(0, 22.73) * mm, "radius": 7.5 * mm, "construction": true});
            skLineSegment(sketch, "E36.0.5.47", {"start": v(-7.5, 22.73) * mm, "end": v(-3.75, 29.22) * mm});
            skLineSegment(sketch, "E36.0.5.48", {"start": v(-61.16, 8.74) * mm, "end": v(-68.66, 8.74) * mm});
            skLineSegment(sketch, "E36.0.5.49", {"start": v(-16.73, 8.74) * mm, "end": v(-9.23, 8.74) * mm});
            skLineSegment(sketch, "E36.0.5.50", {"start": v(-59.43, 22.73) * mm, "end": v(-55.68, 16.23) * mm});
            skLineSegment(sketch, "E36.0.5.51", {"start": v(-68.66, 21.73) * mm, "end": v(-61.16, 21.73) * mm});
            skLineSegment(sketch, "E36.0.5.52", {"start": v(-68.66, 8.74) * mm, "end": v(-72.41, 15.23) * mm});
            skLineSegment(sketch, "E36.0.5.53", {"start": v(-64.91, 15.23) * mm, "end": v(-51.93, 22.73) * mm, "construction": true});
            skLineSegment(sketch, "E36.0.5.54", {"start": v(-38.95, 15.23) * mm, "end": v(-12.98, 15.23) * mm, "construction": true});
            skLineSegment(sketch, "E36.0.5.55", {"start": v(-35.2, 21.73) * mm, "end": v(-31.45, 15.23) * mm});
            skLineSegment(sketch, "E36.0.6.0", {"start": v(-29.71, 44.21) * mm, "end": v(-22.21, 44.21) * mm});
            skLineSegment(sketch, "E36.0.6.1", {"start": v(-33.46, 37.72) * mm, "end": v(-29.71, 44.21) * mm});
            skLineSegment(sketch, "E36.0.6.2", {"start": v(-18.46, 37.72) * mm, "end": v(-22.21, 31.22) * mm});
            skLineSegment(sketch, "E36.0.6.3", {"start": v(-46.45, 30.22) * mm, "end": v(-42.7, 36.72) * mm});
            skCircle(sketch, "E36.0.6.4", {"center": v(-51.93, 37.72) * mm, "radius": 7.5 * mm, "construction": true});
            skLineSegment(sketch, "E36.0.6.5", {"start": v(9.23, 36.72) * mm, "end": v(5.48, 30.22) * mm});
            skLineSegment(sketch, "E36.0.6.6", {"start": v(-12.98, 30.22) * mm, "end": v(-25.96, 37.72) * mm, "construction": true});
            skCircle(sketch, "E36.0.6.7", {"center": v(12.98, 30.22) * mm, "radius": 7.5 * mm, "construction": true});
            skLineSegment(sketch, "E36.0.6.8", {"start": v(-38.95, 30.22) * mm, "end": v(-25.96, 37.72) * mm, "construction": true});
            skLineSegment(sketch, "E36.0.6.9", {"start": v(-16.73, 36.72) * mm, "end": v(-20.48, 30.22) * mm});
            skCircle(sketch, "E36.0.6.10", {"center": v(-64.91, 30.22) * mm, "radius": 7.5 * mm, "construction": true});
            skLineSegment(sketch, "E36.0.6.11", {"start": v(-31.45, 30.22) * mm, "end": v(-35.2, 23.73) * mm});
            skLineSegment(sketch, "E36.0.6.12", {"start": v(7.5, 37.72) * mm, "end": v(3.75, 31.22) * mm});
            skLineSegment(sketch, "E36.0.6.13", {"start": v(9.23, 23.73) * mm, "end": v(16.73, 23.73) * mm});
            skLineSegment(sketch, "E36.0.6.14", {"start": v(3.75, 31.22) * mm, "end": v(-3.75, 31.22) * mm});
            skLineSegment(sketch, "E36.0.6.15", {"start": v(-12.98, 30.22) * mm, "end": v(0, 37.72) * mm, "construction": true});
            skCircle(sketch, "E36.0.6.16", {"center": v(-25.96, 37.72) * mm, "radius": 7.5 * mm, "construction": true});
            skCircle(sketch, "E36.0.6.17", {"center": v(-38.95, 30.22) * mm, "radius": 7.5 * mm, "construction": true});
            skLineSegment(sketch, "E36.0.6.18", {"start": v(-42.7, 36.72) * mm, "end": v(-35.2, 36.72) * mm});
            skLineSegment(sketch, "E36.0.6.19", {"start": v(-29.71, 31.22) * mm, "end": v(-33.46, 37.72) * mm});
            skLineSegment(sketch, "E36.0.6.20", {"start": v(-22.21, 44.21) * mm, "end": v(-18.46, 37.72) * mm});
            skLineSegment(sketch, "E36.0.6.21", {"start": v(-48.18, 31.22) * mm, "end": v(-44.43, 37.72) * mm});
            skLineSegment(sketch, "E36.0.6.22", {"start": v(-57.41, 30.22) * mm, "end": v(-61.16, 23.73) * mm});
            skLineSegment(sketch, "E36.0.6.23", {"start": v(-9.23, 36.72) * mm, "end": v(-16.73, 36.72) * mm});
            skLineSegment(sketch, "E36.0.6.24", {"start": v(3.75, 44.21) * mm, "end": v(7.5, 37.72) * mm});
            skLineSegment(sketch, "E36.0.6.25", {"start": v(20.48, 30.22) * mm, "end": v(16.73, 36.72) * mm});
            skLineSegment(sketch, "E36.0.6.26", {"start": v(16.73, 23.73) * mm, "end": v(20.48, 30.22) * mm});
            skLineSegment(sketch, "E36.0.6.27", {"start": v(-20.48, 30.22) * mm, "end": v(-16.73, 23.73) * mm});
            skLineSegment(sketch, "E36.0.6.28", {"start": v(-72.41, 30.22) * mm, "end": v(-68.66, 36.72) * mm});
            skLineSegment(sketch, "E36.0.6.29", {"start": v(5.48, 30.22) * mm, "end": v(9.23, 23.73) * mm});
            skLineSegment(sketch, "E36.0.6.30", {"start": v(-9.23, 23.73) * mm, "end": v(-5.48, 30.22) * mm});
            skLineSegment(sketch, "E36.0.6.31", {"start": v(-42.7, 23.73) * mm, "end": v(-46.45, 30.22) * mm});
            skLineSegment(sketch, "E36.0.6.32", {"start": v(-55.68, 31.22) * mm, "end": v(-48.18, 31.22) * mm});
            skLineSegment(sketch, "E36.0.6.33", {"start": v(-5.48, 30.22) * mm, "end": v(-9.23, 36.72) * mm});
            skLineSegment(sketch, "E36.0.6.34", {"start": v(-38.95, 30.22) * mm, "end": v(-51.93, 37.72) * mm, "construction": true});
            skLineSegment(sketch, "E36.0.6.35", {"start": v(-44.43, 37.72) * mm, "end": v(-48.18, 44.21) * mm});
            skLineSegment(sketch, "E36.0.6.36", {"start": v(16.73, 36.72) * mm, "end": v(9.23, 36.72) * mm});
            skLineSegment(sketch, "E36.0.6.37", {"start": v(-48.18, 44.21) * mm, "end": v(-55.68, 44.21) * mm});
            skLineSegment(sketch, "E36.0.6.38", {"start": v(-61.16, 36.72) * mm, "end": v(-57.41, 30.22) * mm});
            skLineSegment(sketch, "E36.0.6.39", {"start": v(-35.2, 23.73) * mm, "end": v(-42.7, 23.73) * mm});
            skLineSegment(sketch, "E36.0.6.40", {"start": v(-3.75, 44.21) * mm, "end": v(3.75, 44.21) * mm});
            skLineSegment(sketch, "E36.0.6.41", {"start": v(-3.75, 31.22) * mm, "end": v(-7.5, 37.72) * mm});
            skLineSegment(sketch, "E36.0.6.42", {"start": v(-22.21, 31.22) * mm, "end": v(-29.71, 31.22) * mm});
            skLineSegment(sketch, "E36.0.6.43", {"start": v(12.98, 30.22) * mm, "end": v(0, 37.72) * mm, "construction": true});
            skCircle(sketch, "E36.0.6.44", {"center": v(-12.98, 30.22) * mm, "radius": 7.5 * mm, "construction": true});
            skLineSegment(sketch, "E36.0.6.45", {"start": v(-55.68, 44.21) * mm, "end": v(-59.43, 37.72) * mm});
            skCircle(sketch, "E36.0.6.46", {"center": v(0, 37.72) * mm, "radius": 7.5 * mm, "construction": true});
            skLineSegment(sketch, "E36.0.6.47", {"start": v(-7.5, 37.72) * mm, "end": v(-3.75, 44.21) * mm});
            skLineSegment(sketch, "E36.0.6.48", {"start": v(-61.16, 23.73) * mm, "end": v(-68.66, 23.73) * mm});
            skLineSegment(sketch, "E36.0.6.49", {"start": v(-16.73, 23.73) * mm, "end": v(-9.23, 23.73) * mm});
            skLineSegment(sketch, "E36.0.6.50", {"start": v(-59.43, 37.72) * mm, "end": v(-55.68, 31.22) * mm});
            skLineSegment(sketch, "E36.0.6.51", {"start": v(-68.66, 36.72) * mm, "end": v(-61.16, 36.72) * mm});
            skLineSegment(sketch, "E36.0.6.52", {"start": v(-68.66, 23.73) * mm, "end": v(-72.41, 30.22) * mm});
            skLineSegment(sketch, "E36.0.6.53", {"start": v(-64.91, 30.22) * mm, "end": v(-51.93, 37.72) * mm, "construction": true});
            skLineSegment(sketch, "E36.0.6.54", {"start": v(-38.95, 30.22) * mm, "end": v(-12.98, 30.22) * mm, "construction": true});
            skLineSegment(sketch, "E36.0.6.55", {"start": v(-35.2, 36.72) * mm, "end": v(-31.45, 30.22) * mm});
            skLineSegment(sketch, "E36.0.7.0", {"start": v(-29.71, 59.2) * mm, "end": v(-22.21, 59.2) * mm});
            skLineSegment(sketch, "E36.0.7.1", {"start": v(-33.46, 52.7) * mm, "end": v(-29.71, 59.2) * mm});
            skLineSegment(sketch, "E36.0.7.2", {"start": v(-18.46, 52.7) * mm, "end": v(-22.21, 46.21) * mm});
            skLineSegment(sketch, "E36.0.7.3", {"start": v(-46.45, 45.21) * mm, "end": v(-42.7, 51.7) * mm});
            skCircle(sketch, "E36.0.7.4", {"center": v(-51.93, 52.7) * mm, "radius": 7.5 * mm, "construction": true});
            skLineSegment(sketch, "E36.0.7.5", {"start": v(9.23, 51.7) * mm, "end": v(5.48, 45.21) * mm});
            skLineSegment(sketch, "E36.0.7.6", {"start": v(-12.98, 45.21) * mm, "end": v(-25.96, 52.7) * mm, "construction": true});
            skCircle(sketch, "E36.0.7.7", {"center": v(12.98, 45.21) * mm, "radius": 7.5 * mm, "construction": true});
            skLineSegment(sketch, "E36.0.7.8", {"start": v(-38.95, 45.21) * mm, "end": v(-25.96, 52.7) * mm, "construction": true});
            skLineSegment(sketch, "E36.0.7.9", {"start": v(-16.73, 51.7) * mm, "end": v(-20.48, 45.21) * mm});
            skCircle(sketch, "E36.0.7.10", {"center": v(-64.91, 45.21) * mm, "radius": 7.5 * mm, "construction": true});
            skLineSegment(sketch, "E36.0.7.11", {"start": v(-31.45, 45.21) * mm, "end": v(-35.2, 38.72) * mm});
            skLineSegment(sketch, "E36.0.7.12", {"start": v(7.5, 52.7) * mm, "end": v(3.75, 46.21) * mm});
            skLineSegment(sketch, "E36.0.7.13", {"start": v(9.23, 38.72) * mm, "end": v(16.73, 38.72) * mm});
            skLineSegment(sketch, "E36.0.7.14", {"start": v(3.75, 46.21) * mm, "end": v(-3.75, 46.21) * mm});
            skLineSegment(sketch, "E36.0.7.15", {"start": v(-12.98, 45.21) * mm, "end": v(0, 52.7) * mm, "construction": true});
            skCircle(sketch, "E36.0.7.16", {"center": v(-25.96, 52.7) * mm, "radius": 7.5 * mm, "construction": true});
            skCircle(sketch, "E36.0.7.17", {"center": v(-38.95, 45.21) * mm, "radius": 7.5 * mm, "construction": true});
            skLineSegment(sketch, "E36.0.7.18", {"start": v(-42.7, 51.7) * mm, "end": v(-35.2, 51.7) * mm});
            skLineSegment(sketch, "E36.0.7.19", {"start": v(-29.71, 46.21) * mm, "end": v(-33.46, 52.7) * mm});
            skLineSegment(sketch, "E36.0.7.20", {"start": v(-22.21, 59.2) * mm, "end": v(-18.46, 52.7) * mm});
            skLineSegment(sketch, "E36.0.7.21", {"start": v(-48.18, 46.21) * mm, "end": v(-44.43, 52.7) * mm});
            skLineSegment(sketch, "E36.0.7.22", {"start": v(-57.41, 45.21) * mm, "end": v(-61.16, 38.72) * mm});
            skLineSegment(sketch, "E36.0.7.23", {"start": v(-9.23, 51.7) * mm, "end": v(-16.73, 51.7) * mm});
            skLineSegment(sketch, "E36.0.7.24", {"start": v(3.75, 59.2) * mm, "end": v(7.5, 52.7) * mm});
            skLineSegment(sketch, "E36.0.7.25", {"start": v(20.48, 45.21) * mm, "end": v(16.73, 51.7) * mm});
            skLineSegment(sketch, "E36.0.7.26", {"start": v(16.73, 38.72) * mm, "end": v(20.48, 45.21) * mm});
            skLineSegment(sketch, "E36.0.7.27", {"start": v(-20.48, 45.21) * mm, "end": v(-16.73, 38.72) * mm});
            skLineSegment(sketch, "E36.0.7.28", {"start": v(-72.41, 45.21) * mm, "end": v(-68.66, 51.7) * mm});
            skLineSegment(sketch, "E36.0.7.29", {"start": v(5.48, 45.21) * mm, "end": v(9.23, 38.72) * mm});
            skLineSegment(sketch, "E36.0.7.30", {"start": v(-9.23, 38.72) * mm, "end": v(-5.48, 45.21) * mm});
            skLineSegment(sketch, "E36.0.7.31", {"start": v(-42.7, 38.72) * mm, "end": v(-46.45, 45.21) * mm});
            skLineSegment(sketch, "E36.0.7.32", {"start": v(-55.68, 46.21) * mm, "end": v(-48.18, 46.21) * mm});
            skLineSegment(sketch, "E36.0.7.33", {"start": v(-5.48, 45.21) * mm, "end": v(-9.23, 51.7) * mm});
            skLineSegment(sketch, "E36.0.7.34", {"start": v(-38.95, 45.21) * mm, "end": v(-51.93, 52.7) * mm, "construction": true});
            skLineSegment(sketch, "E36.0.7.35", {"start": v(-44.43, 52.7) * mm, "end": v(-48.18, 59.2) * mm});
            skLineSegment(sketch, "E36.0.7.36", {"start": v(16.73, 51.7) * mm, "end": v(9.23, 51.7) * mm});
            skLineSegment(sketch, "E36.0.7.37", {"start": v(-48.18, 59.2) * mm, "end": v(-55.68, 59.2) * mm});
            skLineSegment(sketch, "E36.0.7.38", {"start": v(-61.16, 51.7) * mm, "end": v(-57.41, 45.21) * mm});
            skLineSegment(sketch, "E36.0.7.39", {"start": v(-35.2, 38.72) * mm, "end": v(-42.7, 38.72) * mm});
            skLineSegment(sketch, "E36.0.7.40", {"start": v(-3.75, 59.2) * mm, "end": v(3.75, 59.2) * mm});
            skLineSegment(sketch, "E36.0.7.41", {"start": v(-3.75, 46.21) * mm, "end": v(-7.5, 52.7) * mm});
            skLineSegment(sketch, "E36.0.7.42", {"start": v(-22.21, 46.21) * mm, "end": v(-29.71, 46.21) * mm});
            skLineSegment(sketch, "E36.0.7.43", {"start": v(12.98, 45.21) * mm, "end": v(0, 52.7) * mm, "construction": true});
            skCircle(sketch, "E36.0.7.44", {"center": v(-12.98, 45.21) * mm, "radius": 7.5 * mm, "construction": true});
            skLineSegment(sketch, "E36.0.7.45", {"start": v(-55.68, 59.2) * mm, "end": v(-59.43, 52.7) * mm});
            skCircle(sketch, "E36.0.7.46", {"center": v(0, 52.7) * mm, "radius": 7.5 * mm, "construction": true});
            skLineSegment(sketch, "E36.0.7.47", {"start": v(-7.5, 52.7) * mm, "end": v(-3.75, 59.2) * mm});
            skLineSegment(sketch, "E36.0.7.48", {"start": v(-61.16, 38.72) * mm, "end": v(-68.66, 38.72) * mm});
            skLineSegment(sketch, "E36.0.7.49", {"start": v(-16.73, 38.72) * mm, "end": v(-9.23, 38.72) * mm});
            skLineSegment(sketch, "E36.0.7.50", {"start": v(-59.43, 52.7) * mm, "end": v(-55.68, 46.21) * mm});
            skLineSegment(sketch, "E36.0.7.51", {"start": v(-68.66, 51.7) * mm, "end": v(-61.16, 51.7) * mm});
            skLineSegment(sketch, "E36.0.7.52", {"start": v(-68.66, 38.72) * mm, "end": v(-72.41, 45.21) * mm});
            skLineSegment(sketch, "E36.0.7.53", {"start": v(-64.91, 45.21) * mm, "end": v(-51.93, 52.7) * mm, "construction": true});
            skLineSegment(sketch, "E36.0.7.54", {"start": v(-38.95, 45.21) * mm, "end": v(-12.98, 45.21) * mm, "construction": true});
            skLineSegment(sketch, "E36.0.7.55", {"start": v(-35.2, 51.7) * mm, "end": v(-31.45, 45.21) * mm});
            skLineSegment(sketch, "E36.0.8.0", {"start": v(-29.71, 74.2) * mm, "end": v(-22.21, 74.2) * mm});
            skLineSegment(sketch, "E36.0.8.1", {"start": v(-33.46, 67.7) * mm, "end": v(-29.71, 74.2) * mm});
            skLineSegment(sketch, "E36.0.8.2", {"start": v(-18.46, 67.7) * mm, "end": v(-22.21, 61.2) * mm});
            skLineSegment(sketch, "E36.0.8.3", {"start": v(-46.45, 60.2) * mm, "end": v(-42.7, 66.7) * mm});
            skCircle(sketch, "E36.0.8.4", {"center": v(-51.93, 67.7) * mm, "radius": 7.5 * mm, "construction": true});
            skLineSegment(sketch, "E36.0.8.5", {"start": v(9.23, 66.7) * mm, "end": v(5.48, 60.2) * mm});
            skLineSegment(sketch, "E36.0.8.6", {"start": v(-12.98, 60.2) * mm, "end": v(-25.96, 67.7) * mm, "construction": true});
            skCircle(sketch, "E36.0.8.7", {"center": v(12.98, 60.2) * mm, "radius": 7.5 * mm, "construction": true});
            skLineSegment(sketch, "E36.0.8.8", {"start": v(-38.95, 60.2) * mm, "end": v(-25.96, 67.7) * mm, "construction": true});
            skLineSegment(sketch, "E36.0.8.9", {"start": v(-16.73, 66.7) * mm, "end": v(-20.48, 60.2) * mm});
            skCircle(sketch, "E36.0.8.10", {"center": v(-64.91, 60.2) * mm, "radius": 7.5 * mm, "construction": true});
            skLineSegment(sketch, "E36.0.8.11", {"start": v(-31.45, 60.2) * mm, "end": v(-35.2, 53.7) * mm});
            skLineSegment(sketch, "E36.0.8.12", {"start": v(7.5, 67.7) * mm, "end": v(3.75, 61.2) * mm});
            skLineSegment(sketch, "E36.0.8.13", {"start": v(9.23, 53.7) * mm, "end": v(16.73, 53.7) * mm});
            skLineSegment(sketch, "E36.0.8.14", {"start": v(3.75, 61.2) * mm, "end": v(-3.75, 61.2) * mm});
            skLineSegment(sketch, "E36.0.8.15", {"start": v(-12.98, 60.2) * mm, "end": v(0, 67.7) * mm, "construction": true});
            skCircle(sketch, "E36.0.8.16", {"center": v(-25.96, 67.7) * mm, "radius": 7.5 * mm, "construction": true});
            skCircle(sketch, "E36.0.8.17", {"center": v(-38.95, 60.2) * mm, "radius": 7.5 * mm, "construction": true});
            skLineSegment(sketch, "E36.0.8.18", {"start": v(-42.7, 66.7) * mm, "end": v(-35.2, 66.7) * mm});
            skLineSegment(sketch, "E36.0.8.19", {"start": v(-29.71, 61.2) * mm, "end": v(-33.46, 67.7) * mm});
            skLineSegment(sketch, "E36.0.8.20", {"start": v(-22.21, 74.2) * mm, "end": v(-18.46, 67.7) * mm});
            skLineSegment(sketch, "E36.0.8.21", {"start": v(-48.18, 61.2) * mm, "end": v(-44.43, 67.7) * mm});
            skLineSegment(sketch, "E36.0.8.22", {"start": v(-57.41, 60.2) * mm, "end": v(-61.16, 53.7) * mm});
            skLineSegment(sketch, "E36.0.8.23", {"start": v(-9.23, 66.7) * mm, "end": v(-16.73, 66.7) * mm});
            skLineSegment(sketch, "E36.0.8.24", {"start": v(3.75, 74.2) * mm, "end": v(7.5, 67.7) * mm});
            skLineSegment(sketch, "E36.0.8.25", {"start": v(20.48, 60.2) * mm, "end": v(16.73, 66.7) * mm});
            skLineSegment(sketch, "E36.0.8.26", {"start": v(16.73, 53.7) * mm, "end": v(20.48, 60.2) * mm});
            skLineSegment(sketch, "E36.0.8.27", {"start": v(-20.48, 60.2) * mm, "end": v(-16.73, 53.7) * mm});
            skLineSegment(sketch, "E36.0.8.28", {"start": v(-72.41, 60.2) * mm, "end": v(-68.66, 66.7) * mm});
            skLineSegment(sketch, "E36.0.8.29", {"start": v(5.48, 60.2) * mm, "end": v(9.23, 53.7) * mm});
            skLineSegment(sketch, "E36.0.8.30", {"start": v(-9.23, 53.7) * mm, "end": v(-5.48, 60.2) * mm});
            skLineSegment(sketch, "E36.0.8.31", {"start": v(-42.7, 53.7) * mm, "end": v(-46.45, 60.2) * mm});
            skLineSegment(sketch, "E36.0.8.32", {"start": v(-55.68, 61.2) * mm, "end": v(-48.18, 61.2) * mm});
            skLineSegment(sketch, "E36.0.8.33", {"start": v(-5.48, 60.2) * mm, "end": v(-9.23, 66.7) * mm});
            skLineSegment(sketch, "E36.0.8.34", {"start": v(-38.95, 60.2) * mm, "end": v(-51.93, 67.7) * mm, "construction": true});
            skLineSegment(sketch, "E36.0.8.35", {"start": v(-44.43, 67.7) * mm, "end": v(-48.18, 74.2) * mm});
            skLineSegment(sketch, "E36.0.8.36", {"start": v(16.73, 66.7) * mm, "end": v(9.23, 66.7) * mm});
            skLineSegment(sketch, "E36.0.8.37", {"start": v(-48.18, 74.2) * mm, "end": v(-55.68, 74.2) * mm});
            skLineSegment(sketch, "E36.0.8.38", {"start": v(-61.16, 66.7) * mm, "end": v(-57.41, 60.2) * mm});
            skLineSegment(sketch, "E36.0.8.39", {"start": v(-35.2, 53.7) * mm, "end": v(-42.7, 53.7) * mm});
            skLineSegment(sketch, "E36.0.8.40", {"start": v(-3.75, 74.2) * mm, "end": v(3.75, 74.2) * mm});
            skLineSegment(sketch, "E36.0.8.41", {"start": v(-3.75, 61.2) * mm, "end": v(-7.5, 67.7) * mm});
            skLineSegment(sketch, "E36.0.8.42", {"start": v(-22.21, 61.2) * mm, "end": v(-29.71, 61.2) * mm});
            skLineSegment(sketch, "E36.0.8.43", {"start": v(12.98, 60.2) * mm, "end": v(0, 67.7) * mm, "construction": true});
            skCircle(sketch, "E36.0.8.44", {"center": v(-12.98, 60.2) * mm, "radius": 7.5 * mm, "construction": true});
            skLineSegment(sketch, "E36.0.8.45", {"start": v(-55.68, 74.2) * mm, "end": v(-59.43, 67.7) * mm});
            skCircle(sketch, "E36.0.8.46", {"center": v(0, 67.7) * mm, "radius": 7.5 * mm, "construction": true});
            skLineSegment(sketch, "E36.0.8.47", {"start": v(-7.5, 67.7) * mm, "end": v(-3.75, 74.2) * mm});
            skLineSegment(sketch, "E36.0.8.48", {"start": v(-61.16, 53.7) * mm, "end": v(-68.66, 53.7) * mm});
            skLineSegment(sketch, "E36.0.8.49", {"start": v(-16.73, 53.7) * mm, "end": v(-9.23, 53.7) * mm});
            skLineSegment(sketch, "E36.0.8.50", {"start": v(-59.43, 67.7) * mm, "end": v(-55.68, 61.2) * mm});
            skLineSegment(sketch, "E36.0.8.51", {"start": v(-68.66, 66.7) * mm, "end": v(-61.16, 66.7) * mm});
            skLineSegment(sketch, "E36.0.8.52", {"start": v(-68.66, 53.7) * mm, "end": v(-72.41, 60.2) * mm});
            skLineSegment(sketch, "E36.0.8.53", {"start": v(-64.91, 60.2) * mm, "end": v(-51.93, 67.7) * mm, "construction": true});
            skLineSegment(sketch, "E36.0.8.54", {"start": v(-38.95, 60.2) * mm, "end": v(-12.98, 60.2) * mm, "construction": true});
            skLineSegment(sketch, "E36.0.8.55", {"start": v(-35.2, 66.7) * mm, "end": v(-31.45, 60.2) * mm});
            skLineSegment(sketch, "E36.direction1", {"start": v(-68.66, -66.21) * mm, "end": v(-65.96, -66.21) * mm, "construction": true});
            skLineSegment(sketch, "E36.direction2", {"start": v(-68.66, -66.21) * mm, "end": v(-68.66, -51.22) * mm, "construction": true});
            skLineSegment(sketch, "E37.0.2.0", {"start": v(38.95, -59.72) * mm, "end": v(25.96, -52.22) * mm, "construction": true});
            skLineSegment(sketch, "E37.3.2.0", {"start": v(29.71, -45.73) * mm, "end": v(33.46, -52.22) * mm});
            skLineSegment(sketch, "E37.6.2.0", {"start": v(12.98, -59.72) * mm, "end": v(25.96, -52.22) * mm, "construction": true});
            skLineSegment(sketch, "E37.9.2.0", {"start": v(22.21, -45.73) * mm, "end": v(29.71, -45.73) * mm});
            skLineSegment(sketch, "E37.12.2.0", {"start": v(42.7, -66.21) * mm, "end": v(46.45, -59.72) * mm});
            skLineSegment(sketch, "E37.15.2.0", {"start": v(46.45, -59.72) * mm, "end": v(42.7, -53.22) * mm});
            skLineSegment(sketch, "E37.18.2.0", {"start": v(31.45, -59.72) * mm, "end": v(35.2, -66.21) * mm});
            skCircle(sketch, "E37.21.2.0", {"center": v(25.96, -52.22) * mm, "radius": 7.5 * mm, "construction": true});
            skLineSegment(sketch, "E37.23.2.0", {"start": v(35.2, -53.22) * mm, "end": v(31.45, -59.72) * mm});
            skLineSegment(sketch, "E37.26.2.0", {"start": v(33.46, -52.22) * mm, "end": v(29.71, -58.72) * mm});
            skLineSegment(sketch, "E37.29.2.0", {"start": v(35.2, -66.21) * mm, "end": v(42.7, -66.21) * mm});
            skLineSegment(sketch, "E37.32.2.0", {"start": v(29.71, -58.72) * mm, "end": v(22.21, -58.72) * mm});
            skLineSegment(sketch, "E37.35.2.0", {"start": v(22.21, -58.72) * mm, "end": v(18.46, -52.22) * mm});
            skLineSegment(sketch, "E37.38.2.0", {"start": v(42.7, -53.22) * mm, "end": v(35.2, -53.22) * mm});
            skLineSegment(sketch, "E37.41.2.0", {"start": v(18.46, -52.22) * mm, "end": v(22.21, -45.73) * mm});
            skCircle(sketch, "E37.44.2.0", {"center": v(38.95, -59.72) * mm, "radius": 7.5 * mm, "construction": true});
            skLineSegment(sketch, "E38.0.3.0", {"start": v(64.91, -59.72) * mm, "end": v(51.93, -52.22) * mm, "construction": true});
            skLineSegment(sketch, "E38.3.3.0", {"start": v(55.68, -45.73) * mm, "end": v(59.43, -52.22) * mm});
            skLineSegment(sketch, "E38.6.3.0", {"start": v(38.95, -59.72) * mm, "end": v(51.93, -52.22) * mm, "construction": true});
            skLineSegment(sketch, "E38.9.3.0", {"start": v(48.18, -45.73) * mm, "end": v(55.68, -45.73) * mm});
            skLineSegment(sketch, "E38.12.3.0", {"start": v(68.66, -66.21) * mm, "end": v(72.41, -59.72) * mm});
            skLineSegment(sketch, "E38.15.3.0", {"start": v(72.41, -59.72) * mm, "end": v(68.66, -53.22) * mm});
            skLineSegment(sketch, "E38.18.3.0", {"start": v(57.41, -59.72) * mm, "end": v(61.16, -66.21) * mm});
            skCircle(sketch, "E38.21.3.0", {"center": v(51.93, -52.22) * mm, "radius": 7.5 * mm, "construction": true});
            skLineSegment(sketch, "E38.23.3.0", {"start": v(61.16, -53.22) * mm, "end": v(57.41, -59.72) * mm});
            skLineSegment(sketch, "E38.26.3.0", {"start": v(59.43, -52.22) * mm, "end": v(55.68, -58.72) * mm});
            skLineSegment(sketch, "E38.29.3.0", {"start": v(61.16, -66.21) * mm, "end": v(68.66, -66.21) * mm});
            skLineSegment(sketch, "E38.32.3.0", {"start": v(55.68, -58.72) * mm, "end": v(48.18, -58.72) * mm});
            skLineSegment(sketch, "E38.35.3.0", {"start": v(48.18, -58.72) * mm, "end": v(44.43, -52.22) * mm});
            skLineSegment(sketch, "E38.38.3.0", {"start": v(68.66, -53.22) * mm, "end": v(61.16, -53.22) * mm});
            skLineSegment(sketch, "E38.41.3.0", {"start": v(44.43, -52.22) * mm, "end": v(48.18, -45.73) * mm});
            skCircle(sketch, "E38.44.3.0", {"center": v(64.91, -59.72) * mm, "radius": 7.5 * mm, "construction": true});
            skLineSegment(sketch, "E39.0.1.0", {"start": v(61.16, -51.22) * mm, "end": v(68.66, -51.22) * mm});
            skLineSegment(sketch, "E39.0.1.1", {"start": v(68.66, -38.23) * mm, "end": v(61.16, -38.23) * mm});
            skLineSegment(sketch, "E39.0.1.2", {"start": v(22.21, -30.74) * mm, "end": v(29.71, -30.74) * mm});
            skCircle(sketch, "E39.0.1.3", {"center": v(64.91, -44.73) * mm, "radius": 7.5 * mm, "construction": true});
            skLineSegment(sketch, "E39.0.1.4", {"start": v(57.41, -44.73) * mm, "end": v(61.16, -51.22) * mm});
            skLineSegment(sketch, "E39.0.1.5", {"start": v(38.95, -44.73) * mm, "end": v(51.93, -37.23) * mm, "construction": true});
            skLineSegment(sketch, "E39.0.1.6", {"start": v(42.7, -51.22) * mm, "end": v(46.45, -44.73) * mm});
            skLineSegment(sketch, "E39.0.1.7", {"start": v(29.71, -43.73) * mm, "end": v(22.21, -43.73) * mm});
            skLineSegment(sketch, "E39.0.1.8", {"start": v(35.2, -51.22) * mm, "end": v(42.7, -51.22) * mm});
            skLineSegment(sketch, "E39.0.1.9", {"start": v(68.66, -51.22) * mm, "end": v(72.41, -44.73) * mm});
            skLineSegment(sketch, "E39.0.1.10", {"start": v(29.71, -30.74) * mm, "end": v(33.46, -37.23) * mm});
            skLineSegment(sketch, "E39.0.1.11", {"start": v(64.91, -44.73) * mm, "end": v(51.93, -37.23) * mm, "construction": true});
            skCircle(sketch, "E39.0.1.12", {"center": v(25.96, -37.23) * mm, "radius": 7.5 * mm, "construction": true});
            skLineSegment(sketch, "E39.0.1.13", {"start": v(55.68, -43.73) * mm, "end": v(48.18, -43.73) * mm});
            skLineSegment(sketch, "E39.0.1.14", {"start": v(48.18, -30.74) * mm, "end": v(55.68, -30.74) * mm});
            skLineSegment(sketch, "E39.0.1.15", {"start": v(33.46, -37.23) * mm, "end": v(29.71, -43.73) * mm});
            skLineSegment(sketch, "E39.0.1.16", {"start": v(55.68, -30.74) * mm, "end": v(59.43, -37.23) * mm});
            skCircle(sketch, "E39.0.1.17", {"center": v(38.95, -44.73) * mm, "radius": 7.5 * mm, "construction": true});
            skLineSegment(sketch, "E39.0.1.18", {"start": v(44.43, -37.23) * mm, "end": v(48.18, -30.74) * mm});
            skLineSegment(sketch, "E39.0.1.19", {"start": v(38.95, -44.73) * mm, "end": v(25.96, -37.23) * mm, "construction": true});
            skLineSegment(sketch, "E39.0.1.20", {"start": v(72.41, -44.73) * mm, "end": v(68.66, -38.23) * mm});
            skLineSegment(sketch, "E39.0.1.21", {"start": v(31.45, -44.73) * mm, "end": v(35.2, -51.22) * mm});
            skCircle(sketch, "E39.0.1.22", {"center": v(51.93, -37.23) * mm, "radius": 7.5 * mm, "construction": true});
            skLineSegment(sketch, "E39.0.1.23", {"start": v(42.7, -38.23) * mm, "end": v(35.2, -38.23) * mm});
            skLineSegment(sketch, "E39.0.1.24", {"start": v(48.18, -43.73) * mm, "end": v(44.43, -37.23) * mm});
            skLineSegment(sketch, "E39.0.1.25", {"start": v(59.43, -37.23) * mm, "end": v(55.68, -43.73) * mm});
            skLineSegment(sketch, "E39.0.1.26", {"start": v(12.98, -44.73) * mm, "end": v(25.96, -37.23) * mm, "construction": true});
            skLineSegment(sketch, "E39.0.1.27", {"start": v(46.45, -44.73) * mm, "end": v(42.7, -38.23) * mm});
            skLineSegment(sketch, "E39.0.1.28", {"start": v(61.16, -38.23) * mm, "end": v(57.41, -44.73) * mm});
            skLineSegment(sketch, "E39.0.1.29", {"start": v(35.2, -38.23) * mm, "end": v(31.45, -44.73) * mm});
            skLineSegment(sketch, "E39.0.1.30", {"start": v(18.46, -37.23) * mm, "end": v(22.21, -30.74) * mm});
            skLineSegment(sketch, "E39.0.1.31", {"start": v(22.21, -43.73) * mm, "end": v(18.46, -37.23) * mm});
            skLineSegment(sketch, "E39.0.2.0", {"start": v(61.16, -36.23) * mm, "end": v(68.66, -36.23) * mm});
            skLineSegment(sketch, "E39.0.2.1", {"start": v(68.66, -23.24) * mm, "end": v(61.16, -23.24) * mm});
            skLineSegment(sketch, "E39.0.2.2", {"start": v(22.21, -15.75) * mm, "end": v(29.71, -15.75) * mm});
            skCircle(sketch, "E39.0.2.3", {"center": v(64.91, -29.74) * mm, "radius": 7.5 * mm, "construction": true});
            skLineSegment(sketch, "E39.0.2.4", {"start": v(57.41, -29.74) * mm, "end": v(61.16, -36.23) * mm});
            skLineSegment(sketch, "E39.0.2.5", {"start": v(38.95, -29.74) * mm, "end": v(51.93, -22.24) * mm, "construction": true});
            skLineSegment(sketch, "E39.0.2.6", {"start": v(42.7, -36.23) * mm, "end": v(46.45, -29.74) * mm});
            skLineSegment(sketch, "E39.0.2.7", {"start": v(29.71, -28.74) * mm, "end": v(22.21, -28.74) * mm});
            skLineSegment(sketch, "E39.0.2.8", {"start": v(35.2, -36.23) * mm, "end": v(42.7, -36.23) * mm});
            skLineSegment(sketch, "E39.0.2.9", {"start": v(68.66, -36.23) * mm, "end": v(72.41, -29.74) * mm});
            skLineSegment(sketch, "E39.0.2.10", {"start": v(29.71, -15.75) * mm, "end": v(33.46, -22.24) * mm});
            skLineSegment(sketch, "E39.0.2.11", {"start": v(64.91, -29.74) * mm, "end": v(51.93, -22.24) * mm, "construction": true});
            skCircle(sketch, "E39.0.2.12", {"center": v(25.96, -22.24) * mm, "radius": 7.5 * mm, "construction": true});
            skLineSegment(sketch, "E39.0.2.13", {"start": v(55.68, -28.74) * mm, "end": v(48.18, -28.74) * mm});
            skLineSegment(sketch, "E39.0.2.14", {"start": v(48.18, -15.75) * mm, "end": v(55.68, -15.75) * mm});
            skLineSegment(sketch, "E39.0.2.15", {"start": v(33.46, -22.24) * mm, "end": v(29.71, -28.74) * mm});
            skLineSegment(sketch, "E39.0.2.16", {"start": v(55.68, -15.75) * mm, "end": v(59.43, -22.24) * mm});
            skCircle(sketch, "E39.0.2.17", {"center": v(38.95, -29.74) * mm, "radius": 7.5 * mm, "construction": true});
            skLineSegment(sketch, "E39.0.2.18", {"start": v(44.43, -22.24) * mm, "end": v(48.18, -15.75) * mm});
            skLineSegment(sketch, "E39.0.2.19", {"start": v(38.95, -29.74) * mm, "end": v(25.96, -22.24) * mm, "construction": true});
            skLineSegment(sketch, "E39.0.2.20", {"start": v(72.41, -29.74) * mm, "end": v(68.66, -23.24) * mm});
            skLineSegment(sketch, "E39.0.2.21", {"start": v(31.45, -29.74) * mm, "end": v(35.2, -36.23) * mm});
            skCircle(sketch, "E39.0.2.22", {"center": v(51.93, -22.24) * mm, "radius": 7.5 * mm, "construction": true});
            skLineSegment(sketch, "E39.0.2.23", {"start": v(42.7, -23.24) * mm, "end": v(35.2, -23.24) * mm});
            skLineSegment(sketch, "E39.0.2.24", {"start": v(48.18, -28.74) * mm, "end": v(44.43, -22.24) * mm});
            skLineSegment(sketch, "E39.0.2.25", {"start": v(59.43, -22.24) * mm, "end": v(55.68, -28.74) * mm});
            skLineSegment(sketch, "E39.0.2.26", {"start": v(12.98, -29.74) * mm, "end": v(25.96, -22.24) * mm, "construction": true});
            skLineSegment(sketch, "E39.0.2.27", {"start": v(46.45, -29.74) * mm, "end": v(42.7, -23.24) * mm});
            skLineSegment(sketch, "E39.0.2.28", {"start": v(61.16, -23.24) * mm, "end": v(57.41, -29.74) * mm});
            skLineSegment(sketch, "E39.0.2.29", {"start": v(35.2, -23.24) * mm, "end": v(31.45, -29.74) * mm});
            skLineSegment(sketch, "E39.0.2.30", {"start": v(18.46, -22.24) * mm, "end": v(22.21, -15.75) * mm});
            skLineSegment(sketch, "E39.0.2.31", {"start": v(22.21, -28.74) * mm, "end": v(18.46, -22.24) * mm});
            skLineSegment(sketch, "E39.0.3.0", {"start": v(61.16, -21.24) * mm, "end": v(68.66, -21.24) * mm});
            skLineSegment(sketch, "E39.0.3.1", {"start": v(68.66, -8.25) * mm, "end": v(61.16, -8.25) * mm});
            skLineSegment(sketch, "E39.0.3.2", {"start": v(22.21, -0.76) * mm, "end": v(29.71, -0.76) * mm});
            skCircle(sketch, "E39.0.3.3", {"center": v(64.91, -14.75) * mm, "radius": 7.5 * mm, "construction": true});
            skLineSegment(sketch, "E39.0.3.4", {"start": v(57.41, -14.75) * mm, "end": v(61.16, -21.24) * mm});
            skLineSegment(sketch, "E39.0.3.5", {"start": v(38.95, -14.75) * mm, "end": v(51.93, -7.25) * mm, "construction": true});
            skLineSegment(sketch, "E39.0.3.6", {"start": v(42.7, -21.24) * mm, "end": v(46.45, -14.75) * mm});
            skLineSegment(sketch, "E39.0.3.7", {"start": v(29.71, -13.75) * mm, "end": v(22.21, -13.75) * mm});
            skLineSegment(sketch, "E39.0.3.8", {"start": v(35.2, -21.24) * mm, "end": v(42.7, -21.24) * mm});
            skLineSegment(sketch, "E39.0.3.9", {"start": v(68.66, -21.24) * mm, "end": v(72.41, -14.75) * mm});
            skLineSegment(sketch, "E39.0.3.10", {"start": v(29.71, -0.76) * mm, "end": v(33.46, -7.25) * mm});
            skLineSegment(sketch, "E39.0.3.11", {"start": v(64.91, -14.75) * mm, "end": v(51.93, -7.25) * mm, "construction": true});
            skCircle(sketch, "E39.0.3.12", {"center": v(25.96, -7.25) * mm, "radius": 7.5 * mm, "construction": true});
            skLineSegment(sketch, "E39.0.3.13", {"start": v(55.68, -13.75) * mm, "end": v(48.18, -13.75) * mm});
            skLineSegment(sketch, "E39.0.3.14", {"start": v(48.18, -0.76) * mm, "end": v(55.68, -0.76) * mm});
            skLineSegment(sketch, "E39.0.3.15", {"start": v(33.46, -7.25) * mm, "end": v(29.71, -13.75) * mm});
            skLineSegment(sketch, "E39.0.3.16", {"start": v(55.68, -0.76) * mm, "end": v(59.43, -7.25) * mm});
            skCircle(sketch, "E39.0.3.17", {"center": v(38.95, -14.75) * mm, "radius": 7.5 * mm, "construction": true});
            skLineSegment(sketch, "E39.0.3.18", {"start": v(44.43, -7.25) * mm, "end": v(48.18, -0.76) * mm});
            skLineSegment(sketch, "E39.0.3.19", {"start": v(38.95, -14.75) * mm, "end": v(25.96, -7.25) * mm, "construction": true});
            skLineSegment(sketch, "E39.0.3.20", {"start": v(72.41, -14.75) * mm, "end": v(68.66, -8.25) * mm});
            skLineSegment(sketch, "E39.0.3.21", {"start": v(31.45, -14.75) * mm, "end": v(35.2, -21.24) * mm});
            skCircle(sketch, "E39.0.3.22", {"center": v(51.93, -7.25) * mm, "radius": 7.5 * mm, "construction": true});
            skLineSegment(sketch, "E39.0.3.23", {"start": v(42.7, -8.25) * mm, "end": v(35.2, -8.25) * mm});
            skLineSegment(sketch, "E39.0.3.24", {"start": v(48.18, -13.75) * mm, "end": v(44.43, -7.25) * mm});
            skLineSegment(sketch, "E39.0.3.25", {"start": v(59.43, -7.25) * mm, "end": v(55.68, -13.75) * mm});
            skLineSegment(sketch, "E39.0.3.26", {"start": v(12.98, -14.75) * mm, "end": v(25.96, -7.25) * mm, "construction": true});
            skLineSegment(sketch, "E39.0.3.27", {"start": v(46.45, -14.75) * mm, "end": v(42.7, -8.25) * mm});
            skLineSegment(sketch, "E39.0.3.28", {"start": v(61.16, -8.25) * mm, "end": v(57.41, -14.75) * mm});
            skLineSegment(sketch, "E39.0.3.29", {"start": v(35.2, -8.25) * mm, "end": v(31.45, -14.75) * mm});
            skLineSegment(sketch, "E39.0.3.30", {"start": v(18.46, -7.25) * mm, "end": v(22.21, -0.76) * mm});
            skLineSegment(sketch, "E39.0.3.31", {"start": v(22.21, -13.75) * mm, "end": v(18.46, -7.25) * mm});
            skLineSegment(sketch, "E39.0.4.0", {"start": v(61.16, -6.25) * mm, "end": v(68.66, -6.25) * mm});
            skLineSegment(sketch, "E39.0.4.1", {"start": v(68.66, 6.74) * mm, "end": v(61.16, 6.74) * mm});
            skLineSegment(sketch, "E39.0.4.2", {"start": v(22.21, 14.23) * mm, "end": v(29.71, 14.23) * mm});
            skCircle(sketch, "E39.0.4.3", {"center": v(64.91, 0.24) * mm, "radius": 7.5 * mm, "construction": true});
            skLineSegment(sketch, "E39.0.4.4", {"start": v(57.41, 0.24) * mm, "end": v(61.16, -6.25) * mm});
            skLineSegment(sketch, "E39.0.4.5", {"start": v(38.95, 0.24) * mm, "end": v(51.93, 7.74) * mm, "construction": true});
            skLineSegment(sketch, "E39.0.4.6", {"start": v(42.7, -6.25) * mm, "end": v(46.45, 0.24) * mm});
            skLineSegment(sketch, "E39.0.4.7", {"start": v(29.71, 1.24) * mm, "end": v(22.21, 1.24) * mm});
            skLineSegment(sketch, "E39.0.4.8", {"start": v(35.2, -6.25) * mm, "end": v(42.7, -6.25) * mm});
            skLineSegment(sketch, "E39.0.4.9", {"start": v(68.66, -6.25) * mm, "end": v(72.41, 0.24) * mm});
            skLineSegment(sketch, "E39.0.4.10", {"start": v(29.71, 14.23) * mm, "end": v(33.46, 7.74) * mm});
            skLineSegment(sketch, "E39.0.4.11", {"start": v(64.91, 0.24) * mm, "end": v(51.93, 7.74) * mm, "construction": true});
            skCircle(sketch, "E39.0.4.12", {"center": v(25.96, 7.74) * mm, "radius": 7.5 * mm, "construction": true});
            skLineSegment(sketch, "E39.0.4.13", {"start": v(55.68, 1.24) * mm, "end": v(48.18, 1.24) * mm});
            skLineSegment(sketch, "E39.0.4.14", {"start": v(48.18, 14.23) * mm, "end": v(55.68, 14.23) * mm});
            skLineSegment(sketch, "E39.0.4.15", {"start": v(33.46, 7.74) * mm, "end": v(29.71, 1.24) * mm});
            skLineSegment(sketch, "E39.0.4.16", {"start": v(55.68, 14.23) * mm, "end": v(59.43, 7.74) * mm});
            skCircle(sketch, "E39.0.4.17", {"center": v(38.95, 0.24) * mm, "radius": 7.5 * mm, "construction": true});
            skLineSegment(sketch, "E39.0.4.18", {"start": v(44.43, 7.74) * mm, "end": v(48.18, 14.23) * mm});
            skLineSegment(sketch, "E39.0.4.19", {"start": v(38.95, 0.24) * mm, "end": v(25.96, 7.74) * mm, "construction": true});
            skLineSegment(sketch, "E39.0.4.20", {"start": v(72.41, 0.24) * mm, "end": v(68.66, 6.74) * mm});
            skLineSegment(sketch, "E39.0.4.21", {"start": v(31.45, 0.24) * mm, "end": v(35.2, -6.25) * mm});
            skCircle(sketch, "E39.0.4.22", {"center": v(51.93, 7.74) * mm, "radius": 7.5 * mm, "construction": true});
            skLineSegment(sketch, "E39.0.4.23", {"start": v(42.7, 6.74) * mm, "end": v(35.2, 6.74) * mm});
            skLineSegment(sketch, "E39.0.4.24", {"start": v(48.18, 1.24) * mm, "end": v(44.43, 7.74) * mm});
            skLineSegment(sketch, "E39.0.4.25", {"start": v(59.43, 7.74) * mm, "end": v(55.68, 1.24) * mm});
            skLineSegment(sketch, "E39.0.4.26", {"start": v(12.98, 0.24) * mm, "end": v(25.96, 7.74) * mm, "construction": true});
            skLineSegment(sketch, "E39.0.4.27", {"start": v(46.45, 0.24) * mm, "end": v(42.7, 6.74) * mm});
            skLineSegment(sketch, "E39.0.4.28", {"start": v(61.16, 6.74) * mm, "end": v(57.41, 0.24) * mm});
            skLineSegment(sketch, "E39.0.4.29", {"start": v(35.2, 6.74) * mm, "end": v(31.45, 0.24) * mm});
            skLineSegment(sketch, "E39.0.4.30", {"start": v(18.46, 7.74) * mm, "end": v(22.21, 14.23) * mm});
            skLineSegment(sketch, "E39.0.4.31", {"start": v(22.21, 1.24) * mm, "end": v(18.46, 7.74) * mm});
            skLineSegment(sketch, "E39.0.5.0", {"start": v(61.16, 8.74) * mm, "end": v(68.66, 8.74) * mm});
            skLineSegment(sketch, "E39.0.5.1", {"start": v(68.66, 21.73) * mm, "end": v(61.16, 21.73) * mm});
            skLineSegment(sketch, "E39.0.5.2", {"start": v(22.21, 29.22) * mm, "end": v(29.71, 29.22) * mm});
            skCircle(sketch, "E39.0.5.3", {"center": v(64.91, 15.23) * mm, "radius": 7.5 * mm, "construction": true});
            skLineSegment(sketch, "E39.0.5.4", {"start": v(57.41, 15.23) * mm, "end": v(61.16, 8.74) * mm});
            skLineSegment(sketch, "E39.0.5.5", {"start": v(38.95, 15.23) * mm, "end": v(51.93, 22.73) * mm, "construction": true});
            skLineSegment(sketch, "E39.0.5.6", {"start": v(42.7, 8.74) * mm, "end": v(46.45, 15.23) * mm});
            skLineSegment(sketch, "E39.0.5.7", {"start": v(29.71, 16.23) * mm, "end": v(22.21, 16.23) * mm});
            skLineSegment(sketch, "E39.0.5.8", {"start": v(35.2, 8.74) * mm, "end": v(42.7, 8.74) * mm});
            skLineSegment(sketch, "E39.0.5.9", {"start": v(68.66, 8.74) * mm, "end": v(72.41, 15.23) * mm});
            skLineSegment(sketch, "E39.0.5.10", {"start": v(29.71, 29.22) * mm, "end": v(33.46, 22.73) * mm});
            skLineSegment(sketch, "E39.0.5.11", {"start": v(64.91, 15.23) * mm, "end": v(51.93, 22.73) * mm, "construction": true});
            skCircle(sketch, "E39.0.5.12", {"center": v(25.96, 22.73) * mm, "radius": 7.5 * mm, "construction": true});
            skLineSegment(sketch, "E39.0.5.13", {"start": v(55.68, 16.23) * mm, "end": v(48.18, 16.23) * mm});
            skLineSegment(sketch, "E39.0.5.14", {"start": v(48.18, 29.22) * mm, "end": v(55.68, 29.22) * mm});
            skLineSegment(sketch, "E39.0.5.15", {"start": v(33.46, 22.73) * mm, "end": v(29.71, 16.23) * mm});
            skLineSegment(sketch, "E39.0.5.16", {"start": v(55.68, 29.22) * mm, "end": v(59.43, 22.73) * mm});
            skCircle(sketch, "E39.0.5.17", {"center": v(38.95, 15.23) * mm, "radius": 7.5 * mm, "construction": true});
            skLineSegment(sketch, "E39.0.5.18", {"start": v(44.43, 22.73) * mm, "end": v(48.18, 29.22) * mm});
            skLineSegment(sketch, "E39.0.5.19", {"start": v(38.95, 15.23) * mm, "end": v(25.96, 22.73) * mm, "construction": true});
            skLineSegment(sketch, "E39.0.5.20", {"start": v(72.41, 15.23) * mm, "end": v(68.66, 21.73) * mm});
            skLineSegment(sketch, "E39.0.5.21", {"start": v(31.45, 15.23) * mm, "end": v(35.2, 8.74) * mm});
            skCircle(sketch, "E39.0.5.22", {"center": v(51.93, 22.73) * mm, "radius": 7.5 * mm, "construction": true});
            skLineSegment(sketch, "E39.0.5.23", {"start": v(42.7, 21.73) * mm, "end": v(35.2, 21.73) * mm});
            skLineSegment(sketch, "E39.0.5.24", {"start": v(48.18, 16.23) * mm, "end": v(44.43, 22.73) * mm});
            skLineSegment(sketch, "E39.0.5.25", {"start": v(59.43, 22.73) * mm, "end": v(55.68, 16.23) * mm});
            skLineSegment(sketch, "E39.0.5.26", {"start": v(12.98, 15.23) * mm, "end": v(25.96, 22.73) * mm, "construction": true});
            skLineSegment(sketch, "E39.0.5.27", {"start": v(46.45, 15.23) * mm, "end": v(42.7, 21.73) * mm});
            skLineSegment(sketch, "E39.0.5.28", {"start": v(61.16, 21.73) * mm, "end": v(57.41, 15.23) * mm});
            skLineSegment(sketch, "E39.0.5.29", {"start": v(35.2, 21.73) * mm, "end": v(31.45, 15.23) * mm});
            skLineSegment(sketch, "E39.0.5.30", {"start": v(18.46, 22.73) * mm, "end": v(22.21, 29.22) * mm});
            skLineSegment(sketch, "E39.0.5.31", {"start": v(22.21, 16.23) * mm, "end": v(18.46, 22.73) * mm});
            skLineSegment(sketch, "E39.0.6.0", {"start": v(61.16, 23.73) * mm, "end": v(68.66, 23.73) * mm});
            skLineSegment(sketch, "E39.0.6.1", {"start": v(68.66, 36.72) * mm, "end": v(61.16, 36.72) * mm});
            skLineSegment(sketch, "E39.0.6.2", {"start": v(22.21, 44.21) * mm, "end": v(29.71, 44.21) * mm});
            skCircle(sketch, "E39.0.6.3", {"center": v(64.91, 30.22) * mm, "radius": 7.5 * mm, "construction": true});
            skLineSegment(sketch, "E39.0.6.4", {"start": v(57.41, 30.22) * mm, "end": v(61.16, 23.73) * mm});
            skLineSegment(sketch, "E39.0.6.5", {"start": v(38.95, 30.22) * mm, "end": v(51.93, 37.72) * mm, "construction": true});
            skLineSegment(sketch, "E39.0.6.6", {"start": v(42.7, 23.73) * mm, "end": v(46.45, 30.22) * mm});
            skLineSegment(sketch, "E39.0.6.7", {"start": v(29.71, 31.22) * mm, "end": v(22.21, 31.22) * mm});
            skLineSegment(sketch, "E39.0.6.8", {"start": v(35.2, 23.73) * mm, "end": v(42.7, 23.73) * mm});
            skLineSegment(sketch, "E39.0.6.9", {"start": v(68.66, 23.73) * mm, "end": v(72.41, 30.22) * mm});
            skLineSegment(sketch, "E39.0.6.10", {"start": v(29.71, 44.21) * mm, "end": v(33.46, 37.72) * mm});
            skLineSegment(sketch, "E39.0.6.11", {"start": v(64.91, 30.22) * mm, "end": v(51.93, 37.72) * mm, "construction": true});
            skCircle(sketch, "E39.0.6.12", {"center": v(25.96, 37.72) * mm, "radius": 7.5 * mm, "construction": true});
            skLineSegment(sketch, "E39.0.6.13", {"start": v(55.68, 31.22) * mm, "end": v(48.18, 31.22) * mm});
            skLineSegment(sketch, "E39.0.6.14", {"start": v(48.18, 44.21) * mm, "end": v(55.68, 44.21) * mm});
            skLineSegment(sketch, "E39.0.6.15", {"start": v(33.46, 37.72) * mm, "end": v(29.71, 31.22) * mm});
            skLineSegment(sketch, "E39.0.6.16", {"start": v(55.68, 44.21) * mm, "end": v(59.43, 37.72) * mm});
            skCircle(sketch, "E39.0.6.17", {"center": v(38.95, 30.22) * mm, "radius": 7.5 * mm, "construction": true});
            skLineSegment(sketch, "E39.0.6.18", {"start": v(44.43, 37.72) * mm, "end": v(48.18, 44.21) * mm});
            skLineSegment(sketch, "E39.0.6.19", {"start": v(38.95, 30.22) * mm, "end": v(25.96, 37.72) * mm, "construction": true});
            skLineSegment(sketch, "E39.0.6.20", {"start": v(72.41, 30.22) * mm, "end": v(68.66, 36.72) * mm});
            skLineSegment(sketch, "E39.0.6.21", {"start": v(31.45, 30.22) * mm, "end": v(35.2, 23.73) * mm});
            skCircle(sketch, "E39.0.6.22", {"center": v(51.93, 37.72) * mm, "radius": 7.5 * mm, "construction": true});
            skLineSegment(sketch, "E39.0.6.23", {"start": v(42.7, 36.72) * mm, "end": v(35.2, 36.72) * mm});
            skLineSegment(sketch, "E39.0.6.24", {"start": v(48.18, 31.22) * mm, "end": v(44.43, 37.72) * mm});
            skLineSegment(sketch, "E39.0.6.25", {"start": v(59.43, 37.72) * mm, "end": v(55.68, 31.22) * mm});
            skLineSegment(sketch, "E39.0.6.26", {"start": v(12.98, 30.22) * mm, "end": v(25.96, 37.72) * mm, "construction": true});
            skLineSegment(sketch, "E39.0.6.27", {"start": v(46.45, 30.22) * mm, "end": v(42.7, 36.72) * mm});
            skLineSegment(sketch, "E39.0.6.28", {"start": v(61.16, 36.72) * mm, "end": v(57.41, 30.22) * mm});
            skLineSegment(sketch, "E39.0.6.29", {"start": v(35.2, 36.72) * mm, "end": v(31.45, 30.22) * mm});
            skLineSegment(sketch, "E39.0.6.30", {"start": v(18.46, 37.72) * mm, "end": v(22.21, 44.21) * mm});
            skLineSegment(sketch, "E39.0.6.31", {"start": v(22.21, 31.22) * mm, "end": v(18.46, 37.72) * mm});
            skLineSegment(sketch, "E39.0.7.0", {"start": v(61.16, 38.72) * mm, "end": v(68.66, 38.72) * mm});
            skLineSegment(sketch, "E39.0.7.1", {"start": v(68.66, 51.7) * mm, "end": v(61.16, 51.7) * mm});
            skLineSegment(sketch, "E39.0.7.2", {"start": v(22.21, 59.2) * mm, "end": v(29.71, 59.2) * mm});
            skCircle(sketch, "E39.0.7.3", {"center": v(64.91, 45.21) * mm, "radius": 7.5 * mm, "construction": true});
            skLineSegment(sketch, "E39.0.7.4", {"start": v(57.41, 45.21) * mm, "end": v(61.16, 38.72) * mm});
            skLineSegment(sketch, "E39.0.7.5", {"start": v(38.95, 45.21) * mm, "end": v(51.93, 52.7) * mm, "construction": true});
            skLineSegment(sketch, "E39.0.7.6", {"start": v(42.7, 38.72) * mm, "end": v(46.45, 45.21) * mm});
            skLineSegment(sketch, "E39.0.7.7", {"start": v(29.71, 46.21) * mm, "end": v(22.21, 46.21) * mm});
            skLineSegment(sketch, "E39.0.7.8", {"start": v(35.2, 38.72) * mm, "end": v(42.7, 38.72) * mm});
            skLineSegment(sketch, "E39.0.7.9", {"start": v(68.66, 38.72) * mm, "end": v(72.41, 45.21) * mm});
            skLineSegment(sketch, "E39.0.7.10", {"start": v(29.71, 59.2) * mm, "end": v(33.46, 52.7) * mm});
            skLineSegment(sketch, "E39.0.7.11", {"start": v(64.91, 45.21) * mm, "end": v(51.93, 52.7) * mm, "construction": true});
            skCircle(sketch, "E39.0.7.12", {"center": v(25.96, 52.7) * mm, "radius": 7.5 * mm, "construction": true});
            skLineSegment(sketch, "E39.0.7.13", {"start": v(55.68, 46.21) * mm, "end": v(48.18, 46.21) * mm});
            skLineSegment(sketch, "E39.0.7.14", {"start": v(48.18, 59.2) * mm, "end": v(55.68, 59.2) * mm});
            skLineSegment(sketch, "E39.0.7.15", {"start": v(33.46, 52.7) * mm, "end": v(29.71, 46.21) * mm});
            skLineSegment(sketch, "E39.0.7.16", {"start": v(55.68, 59.2) * mm, "end": v(59.43, 52.7) * mm});
            skCircle(sketch, "E39.0.7.17", {"center": v(38.95, 45.21) * mm, "radius": 7.5 * mm, "construction": true});
            skLineSegment(sketch, "E39.0.7.18", {"start": v(44.43, 52.7) * mm, "end": v(48.18, 59.2) * mm});
            skLineSegment(sketch, "E39.0.7.19", {"start": v(38.95, 45.21) * mm, "end": v(25.96, 52.7) * mm, "construction": true});
            skLineSegment(sketch, "E39.0.7.20", {"start": v(72.41, 45.21) * mm, "end": v(68.66, 51.7) * mm});
            skLineSegment(sketch, "E39.0.7.21", {"start": v(31.45, 45.21) * mm, "end": v(35.2, 38.72) * mm});
            skCircle(sketch, "E39.0.7.22", {"center": v(51.93, 52.7) * mm, "radius": 7.5 * mm, "construction": true});
            skLineSegment(sketch, "E39.0.7.23", {"start": v(42.7, 51.7) * mm, "end": v(35.2, 51.7) * mm});
            skLineSegment(sketch, "E39.0.7.24", {"start": v(48.18, 46.21) * mm, "end": v(44.43, 52.7) * mm});
            skLineSegment(sketch, "E39.0.7.25", {"start": v(59.43, 52.7) * mm, "end": v(55.68, 46.21) * mm});
            skLineSegment(sketch, "E39.0.7.26", {"start": v(12.98, 45.21) * mm, "end": v(25.96, 52.7) * mm, "construction": true});
            skLineSegment(sketch, "E39.0.7.27", {"start": v(46.45, 45.21) * mm, "end": v(42.7, 51.7) * mm});
            skLineSegment(sketch, "E39.0.7.28", {"start": v(61.16, 51.7) * mm, "end": v(57.41, 45.21) * mm});
            skLineSegment(sketch, "E39.0.7.29", {"start": v(35.2, 51.7) * mm, "end": v(31.45, 45.21) * mm});
            skLineSegment(sketch, "E39.0.7.30", {"start": v(18.46, 52.7) * mm, "end": v(22.21, 59.2) * mm});
            skLineSegment(sketch, "E39.0.7.31", {"start": v(22.21, 46.21) * mm, "end": v(18.46, 52.7) * mm});
            skLineSegment(sketch, "E39.0.8.0", {"start": v(61.16, 53.7) * mm, "end": v(68.66, 53.7) * mm});
            skLineSegment(sketch, "E39.0.8.1", {"start": v(68.66, 66.7) * mm, "end": v(61.16, 66.7) * mm});
            skLineSegment(sketch, "E39.0.8.2", {"start": v(22.21, 74.2) * mm, "end": v(29.71, 74.2) * mm});
            skCircle(sketch, "E39.0.8.3", {"center": v(64.91, 60.2) * mm, "radius": 7.5 * mm, "construction": true});
            skLineSegment(sketch, "E39.0.8.4", {"start": v(57.41, 60.2) * mm, "end": v(61.16, 53.7) * mm});
            skLineSegment(sketch, "E39.0.8.5", {"start": v(38.95, 60.2) * mm, "end": v(51.93, 67.7) * mm, "construction": true});
            skLineSegment(sketch, "E39.0.8.6", {"start": v(42.7, 53.7) * mm, "end": v(46.45, 60.2) * mm});
            skLineSegment(sketch, "E39.0.8.7", {"start": v(29.71, 61.2) * mm, "end": v(22.21, 61.2) * mm});
            skLineSegment(sketch, "E39.0.8.8", {"start": v(35.2, 53.7) * mm, "end": v(42.7, 53.7) * mm});
            skLineSegment(sketch, "E39.0.8.9", {"start": v(68.66, 53.7) * mm, "end": v(72.41, 60.2) * mm});
            skLineSegment(sketch, "E39.0.8.10", {"start": v(29.71, 74.2) * mm, "end": v(33.46, 67.7) * mm});
            skLineSegment(sketch, "E39.0.8.11", {"start": v(64.91, 60.2) * mm, "end": v(51.93, 67.7) * mm, "construction": true});
            skCircle(sketch, "E39.0.8.12", {"center": v(25.96, 67.7) * mm, "radius": 7.5 * mm, "construction": true});
            skLineSegment(sketch, "E39.0.8.13", {"start": v(55.68, 61.2) * mm, "end": v(48.18, 61.2) * mm});
            skLineSegment(sketch, "E39.0.8.14", {"start": v(48.18, 74.2) * mm, "end": v(55.68, 74.2) * mm});
            skLineSegment(sketch, "E39.0.8.15", {"start": v(33.46, 67.7) * mm, "end": v(29.71, 61.2) * mm});
            skLineSegment(sketch, "E39.0.8.16", {"start": v(55.68, 74.2) * mm, "end": v(59.43, 67.7) * mm});
            skCircle(sketch, "E39.0.8.17", {"center": v(38.95, 60.2) * mm, "radius": 7.5 * mm, "construction": true});
            skLineSegment(sketch, "E39.0.8.18", {"start": v(44.43, 67.7) * mm, "end": v(48.18, 74.2) * mm});
            skLineSegment(sketch, "E39.0.8.19", {"start": v(38.95, 60.2) * mm, "end": v(25.96, 67.7) * mm, "construction": true});
            skLineSegment(sketch, "E39.0.8.20", {"start": v(72.41, 60.2) * mm, "end": v(68.66, 66.7) * mm});
            skLineSegment(sketch, "E39.0.8.21", {"start": v(31.45, 60.2) * mm, "end": v(35.2, 53.7) * mm});
            skCircle(sketch, "E39.0.8.22", {"center": v(51.93, 67.7) * mm, "radius": 7.5 * mm, "construction": true});
            skLineSegment(sketch, "E39.0.8.23", {"start": v(42.7, 66.7) * mm, "end": v(35.2, 66.7) * mm});
            skLineSegment(sketch, "E39.0.8.24", {"start": v(48.18, 61.2) * mm, "end": v(44.43, 67.7) * mm});
            skLineSegment(sketch, "E39.0.8.25", {"start": v(59.43, 67.7) * mm, "end": v(55.68, 61.2) * mm});
            skLineSegment(sketch, "E39.0.8.26", {"start": v(12.98, 60.2) * mm, "end": v(25.96, 67.7) * mm, "construction": true});
            skLineSegment(sketch, "E39.0.8.27", {"start": v(46.45, 60.2) * mm, "end": v(42.7, 66.7) * mm});
            skLineSegment(sketch, "E39.0.8.28", {"start": v(61.16, 66.7) * mm, "end": v(57.41, 60.2) * mm});
            skLineSegment(sketch, "E39.0.8.29", {"start": v(35.2, 66.7) * mm, "end": v(31.45, 60.2) * mm});
            skLineSegment(sketch, "E39.0.8.30", {"start": v(18.46, 67.7) * mm, "end": v(22.21, 74.2) * mm});
            skLineSegment(sketch, "E39.0.8.31", {"start": v(22.21, 61.2) * mm, "end": v(18.46, 67.7) * mm});
            skLineSegment(sketch, "E39.direction1", {"start": v(12.98, -59.72) * mm, "end": v(37.98, -59.72) * mm, "construction": true});
            skLineSegment(sketch, "E39.direction2", {"start": v(12.98, -59.72) * mm, "end": v(12.98, -44.73) * mm, "construction": true});
            skLineSegment(sketch, "E40.0.1.0", {"start": v(72.41, -74.7) * mm, "end": v(68.66, -68.21) * mm});
            skLineSegment(sketch, "E40.0.1.1", {"start": v(3.75, -73.7) * mm, "end": v(-3.75, -73.7) * mm});
            skLineSegment(sketch, "E40.0.1.2", {"start": v(22.21, -60.72) * mm, "end": v(29.71, -60.72) * mm});
            skLineSegment(sketch, "E40.0.1.3", {"start": v(-38.95, -74.7) * mm, "end": v(-12.98, -74.7) * mm, "construction": true});
            skLineSegment(sketch, "E40.0.1.4", {"start": v(16.73, -68.21) * mm, "end": v(9.23, -68.21) * mm});
            skLineSegment(sketch, "E40.0.1.5", {"start": v(-5.48, -74.7) * mm, "end": v(-9.23, -68.21) * mm});
            skCircle(sketch, "E40.0.1.6", {"center": v(25.96, -67.21) * mm, "radius": 7.5 * mm, "construction": true});
            skLineSegment(sketch, "E40.0.1.7", {"start": v(55.68, -73.7) * mm, "end": v(48.18, -73.7) * mm});
            skLineSegment(sketch, "E40.0.1.8", {"start": v(-12.98, -74.7) * mm, "end": v(-25.96, -67.21) * mm, "construction": true});
            skLineSegment(sketch, "E40.0.1.9", {"start": v(-16.73, -68.21) * mm, "end": v(-20.48, -74.7) * mm});
            skLineSegment(sketch, "E40.0.1.10", {"start": v(42.7, -68.21) * mm, "end": v(35.2, -68.21) * mm});
            skLineSegment(sketch, "E40.0.1.11", {"start": v(29.71, -73.7) * mm, "end": v(22.21, -73.7) * mm});
            skLineSegment(sketch, "E40.0.1.12", {"start": v(20.48, -74.7) * mm, "end": v(16.73, -68.21) * mm});
            skLineSegment(sketch, "E40.0.1.13", {"start": v(-48.18, -60.72) * mm, "end": v(-55.68, -60.72) * mm});
            skLineSegment(sketch, "E40.0.1.14", {"start": v(-61.16, -68.21) * mm, "end": v(-57.41, -74.7) * mm});
            skLineSegment(sketch, "E40.0.1.15", {"start": v(48.18, -73.7) * mm, "end": v(44.43, -67.21) * mm});
            skLineSegment(sketch, "E40.0.1.16", {"start": v(12.98, -74.7) * mm, "end": v(25.96, -67.21) * mm, "construction": true});
            skLineSegment(sketch, "E40.0.1.17", {"start": v(-44.43, -67.21) * mm, "end": v(-48.18, -60.72) * mm});
            skLineSegment(sketch, "E40.0.1.18", {"start": v(12.98, -74.7) * mm, "end": v(0, -67.21) * mm, "construction": true});
            skLineSegment(sketch, "E40.0.1.19", {"start": v(55.68, -60.72) * mm, "end": v(59.43, -67.21) * mm});
            skLineSegment(sketch, "E40.0.1.20", {"start": v(18.46, -67.21) * mm, "end": v(22.21, -60.72) * mm});
            skLineSegment(sketch, "E40.0.1.21", {"start": v(-35.2, -68.21) * mm, "end": v(-31.45, -74.7) * mm});
            skLineSegment(sketch, "E40.0.1.22", {"start": v(29.71, -60.72) * mm, "end": v(33.46, -67.21) * mm});
            skCircle(sketch, "E40.0.1.23", {"center": v(-25.96, -67.21) * mm, "radius": 7.5 * mm, "construction": true});
            skLineSegment(sketch, "E40.0.1.24", {"start": v(-72.41, -74.7) * mm, "end": v(-68.66, -68.21) * mm});
            skCircle(sketch, "E40.0.1.25", {"center": v(-51.93, -67.21) * mm, "radius": 7.5 * mm, "construction": true});
            skLineSegment(sketch, "E40.0.1.26", {"start": v(-64.91, -74.7) * mm, "end": v(-51.93, -67.21) * mm, "construction": true});
            skLineSegment(sketch, "E40.0.1.27", {"start": v(-22.21, -73.7) * mm, "end": v(-29.71, -73.7) * mm});
            skCircle(sketch, "E40.0.1.28", {"center": v(51.93, -67.21) * mm, "radius": 7.5 * mm, "construction": true});
            skLineSegment(sketch, "E40.0.1.29", {"start": v(9.23, -68.21) * mm, "end": v(5.48, -74.7) * mm});
            skLineSegment(sketch, "E40.0.1.30", {"start": v(3.75, -60.72) * mm, "end": v(7.5, -67.21) * mm});
            skLineSegment(sketch, "E40.0.1.31", {"start": v(-9.23, -68.21) * mm, "end": v(-16.73, -68.21) * mm});
            skLineSegment(sketch, "E40.0.1.32", {"start": v(38.95, -74.7) * mm, "end": v(25.96, -67.21) * mm, "construction": true});
            skLineSegment(sketch, "E40.0.1.33", {"start": v(-55.68, -60.72) * mm, "end": v(-59.43, -67.21) * mm});
            skLineSegment(sketch, "E40.0.1.34", {"start": v(68.66, -68.21) * mm, "end": v(61.16, -68.21) * mm});
            skLineSegment(sketch, "E40.0.1.35", {"start": v(-55.68, -73.7) * mm, "end": v(-48.18, -73.7) * mm});
            skLineSegment(sketch, "E40.0.1.36", {"start": v(-29.71, -73.7) * mm, "end": v(-33.46, -67.21) * mm});
            skLineSegment(sketch, "E40.0.1.37", {"start": v(64.91, -74.7) * mm, "end": v(51.93, -67.21) * mm, "construction": true});
            skLineSegment(sketch, "E40.0.1.38", {"start": v(61.16, -68.21) * mm, "end": v(57.41, -74.7) * mm});
            skLineSegment(sketch, "E40.0.1.39", {"start": v(44.43, -67.21) * mm, "end": v(48.18, -60.72) * mm});
            skLineSegment(sketch, "E40.0.1.40", {"start": v(38.95, -74.7) * mm, "end": v(51.93, -67.21) * mm, "construction": true});
            skLineSegment(sketch, "E40.0.1.41", {"start": v(-7.5, -67.21) * mm, "end": v(-3.75, -60.72) * mm});
            skLineSegment(sketch, "E40.0.1.42", {"start": v(-22.21, -60.72) * mm, "end": v(-18.46, -67.21) * mm});
            skLineSegment(sketch, "E40.0.1.43", {"start": v(46.45, -74.7) * mm, "end": v(42.7, -68.21) * mm});
            skLineSegment(sketch, "E40.0.1.44", {"start": v(-38.95, -74.7) * mm, "end": v(-51.93, -67.21) * mm, "construction": true});
            skLineSegment(sketch, "E40.0.1.45", {"start": v(-12.98, -74.7) * mm, "end": v(0, -67.21) * mm, "construction": true});
            skLineSegment(sketch, "E40.0.1.46", {"start": v(-68.66, -68.21) * mm, "end": v(-61.16, -68.21) * mm});
            skLineSegment(sketch, "E40.0.1.47", {"start": v(-42.7, -68.21) * mm, "end": v(-35.2, -68.21) * mm});
            skLineSegment(sketch, "E40.0.1.48", {"start": v(-3.75, -60.72) * mm, "end": v(3.75, -60.72) * mm});
            skLineSegment(sketch, "E40.0.1.49", {"start": v(48.18, -60.72) * mm, "end": v(55.68, -60.72) * mm});
            skLineSegment(sketch, "E40.0.1.50", {"start": v(-38.95, -74.7) * mm, "end": v(-25.96, -67.21) * mm, "construction": true});
            skLineSegment(sketch, "E40.0.1.51", {"start": v(-33.46, -67.21) * mm, "end": v(-29.71, -60.72) * mm});
            skLineSegment(sketch, "E40.0.1.52", {"start": v(-29.71, -60.72) * mm, "end": v(-22.21, -60.72) * mm});
            skLineSegment(sketch, "E40.0.1.53", {"start": v(-46.45, -74.7) * mm, "end": v(-42.7, -68.21) * mm});
            skLineSegment(sketch, "E40.0.1.54", {"start": v(35.2, -68.21) * mm, "end": v(31.45, -74.7) * mm});
            skCircle(sketch, "E40.0.1.55", {"center": v(0, -67.21) * mm, "radius": 7.5 * mm, "construction": true});
            skLineSegment(sketch, "E40.0.1.56", {"start": v(59.43, -67.21) * mm, "end": v(55.68, -73.7) * mm});
            skLineSegment(sketch, "E40.0.1.57", {"start": v(-18.46, -67.21) * mm, "end": v(-22.21, -73.7) * mm});
            skLineSegment(sketch, "E40.0.1.58", {"start": v(7.5, -67.21) * mm, "end": v(3.75, -73.7) * mm});
            skLineSegment(sketch, "E40.0.1.59", {"start": v(-3.75, -73.7) * mm, "end": v(-7.5, -67.21) * mm});
            skLineSegment(sketch, "E40.0.1.60", {"start": v(33.46, -67.21) * mm, "end": v(29.71, -73.7) * mm});
            skLineSegment(sketch, "E40.0.1.61", {"start": v(22.21, -73.7) * mm, "end": v(18.46, -67.21) * mm});
            skLineSegment(sketch, "E40.0.1.62", {"start": v(-59.43, -67.21) * mm, "end": v(-55.68, -73.7) * mm});
            skLineSegment(sketch, "E40.0.1.63", {"start": v(-48.18, -73.7) * mm, "end": v(-44.43, -67.21) * mm});
            skLineSegment(sketch, "E40.direction1", {"start": v(-72.41, 60.2) * mm, "end": v(-47.41, 60.2) * mm, "construction": true});
            skLineSegment(sketch, "E40.direction2", {"start": v(-72.41, 60.2) * mm, "end": v(-72.41, -74.7) * mm, "construction": true});
            skSolve(sketch);
        }
        {
            var Q0;
            Q0 = qSketchRegion(id + "F2", true);
            extrude(context, id + "F3", {"entities" : qUnion([Q0]), "operationType" : NewBodyOperationType.REMOVE, "offsetDistance" : 25 * mm, "depth" : 25 * mm});
        }
    });
